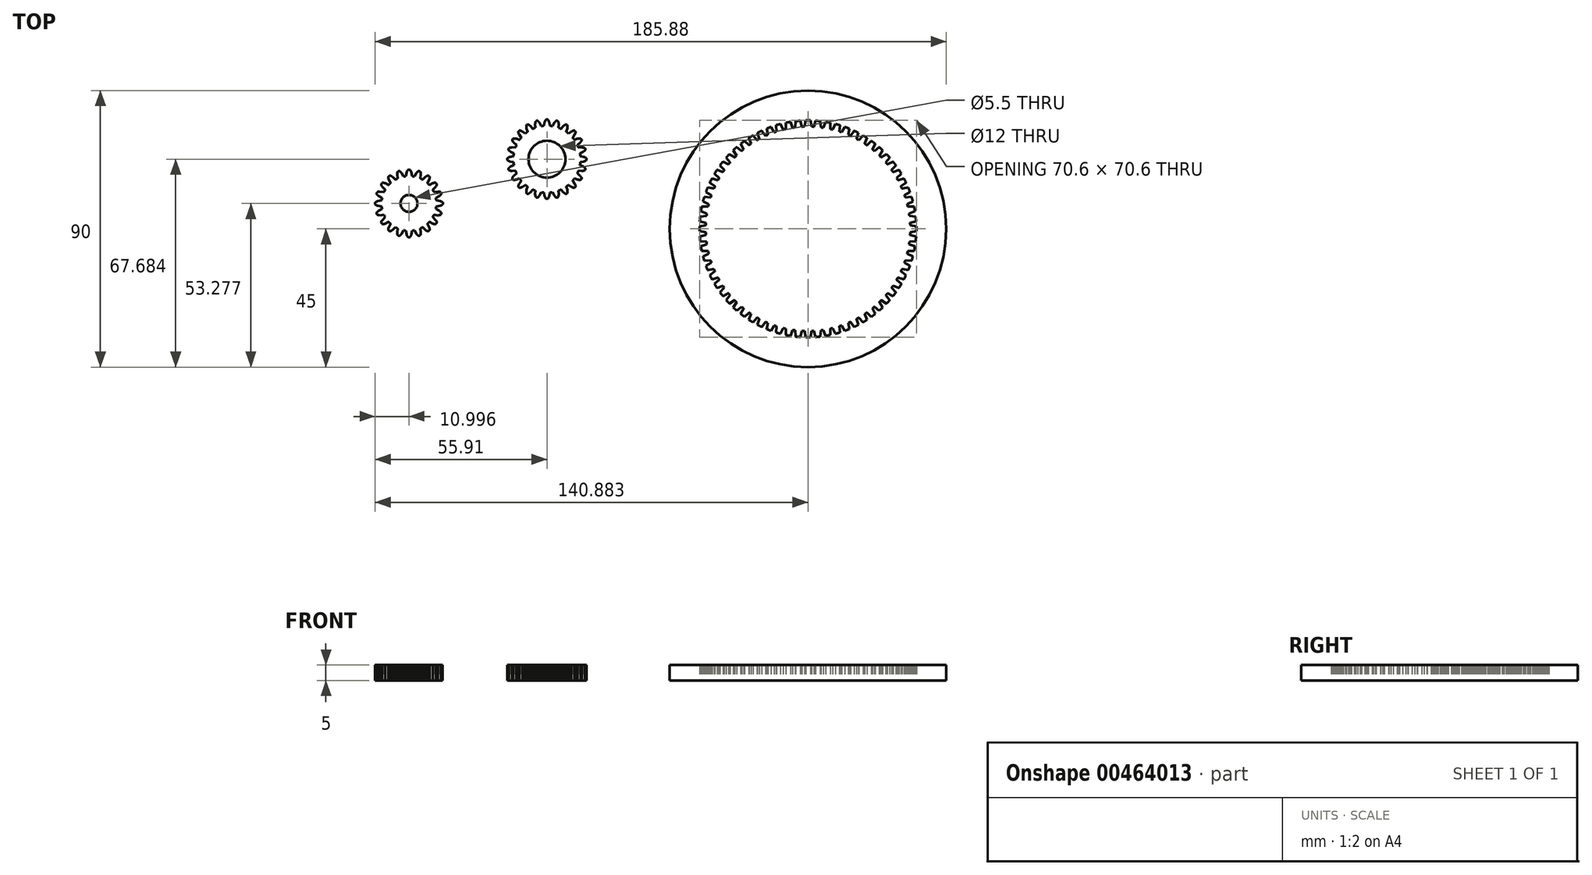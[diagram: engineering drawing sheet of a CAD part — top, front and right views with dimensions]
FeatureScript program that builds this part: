
annotation { "Feature Type Name" : "Feature", "Feature Type Description" : "" }
export const myFeature = defineFeature(function(context is Context, id is Id, definition is map)
    precondition{}
    {
        {
            var Q0;
            Q0=qCreatedBy(makeId("Top.planeOp"),FACE);
            var sketch = newSketch(context, id + "F0", { "sketchPlane" : qUnion([Q0])});
            skLineSegment(sketch, "E0.bottom", {"start": v(15.5, 15.5) * mm, "end": v(-15.5, 15.5) * mm, "construction": true});
            skLineSegment(sketch, "E0.top", {"start": v(15.5, -15.5) * mm, "end": v(-15.5, -15.5) * mm, "construction": true});
            skLineSegment(sketch, "E0.left", {"start": v(15.5, 15.5) * mm, "end": v(15.5, -15.5) * mm, "construction": true});
            skLineSegment(sketch, "E0.right", {"start": v(-15.5, 15.5) * mm, "end": v(-15.5, -15.5) * mm, "construction": true});
            skPoint(sketch, "E0.middle", {"position": v(0, 0) * mm});
            skCircle(sketch, "E1", {"center": v(0, 0) * mm, "radius": 10 * mm});
            skCircle(sketch, "E2", {"center": v(15.5, 15.5) * mm, "radius": 11.92 * mm});
            skCircle(sketch, "E3", {"center": v(15.5, -15.5) * mm, "radius": 11.92 * mm});
            skCircle(sketch, "E4", {"center": v(-15.5, -15.5) * mm, "radius": 11.92 * mm});
            skCircle(sketch, "E5", {"center": v(-15.5, 15.5) * mm, "radius": 11.92 * mm});
            skCircle(sketch, "E6", {"center": v(0, 0) * mm, "radius": 33.84 * mm});
            skCircle(sketch, "E7", {"center": v(0, 0) * mm, "radius": 11 * mm});
            skCircle(sketch, "E8", {"center": v(-15.5, 15.5) * mm, "radius": 12.92 * mm});
            skCircle(sketch, "E9", {"center": v(0, 0) * mm, "radius": 32.84 * mm});
            skPoint(sketch, "E10.center", {"position": v(-0.29, 2.68) * mm});
            skCircle(sketch, "E11", {"center": v(15.5, 15.5) * mm, "radius": 10.92 * mm, "construction": true});
            skCircle(sketch, "E12", {"center": v(15.5, -15.5) * mm, "radius": 10.92 * mm, "construction": true});
            skCircle(sketch, "E13", {"center": v(-15.5, -15.5) * mm, "radius": 10.92 * mm, "construction": true});
            skCircle(sketch, "E14", {"center": v(-15.5, 15.5) * mm, "radius": 10.92 * mm, "construction": true});
            skCircle(sketch, "E15", {"center": v(0, 0) * mm, "radius": 34.77 * mm, "construction": true});
            skCircle(sketch, "E16", {"center": v(0, 0) * mm, "radius": 8.93 * mm, "construction": true});
            skLineSegment(sketch, "E17", {"start": v(-0.79, 0) * mm, "end": v(-0.79, 9.97) * mm, "construction": true});
            skLineSegment(sketch, "E18", {"start": v(0.79, 0) * mm, "end": v(0.79, 9.97) * mm, "construction": true});
            skLineSegment(sketch, "E19", {"start": v(0.6, 10.98) * mm, "end": v(0.79, 9.97) * mm});
            skLineSegment(sketch, "E20", {"start": v(0.79, 9.97) * mm, "end": v(0.98, 8.87) * mm});
            skLineSegment(sketch, "E21", {"start": v(-0.79, 9.97) * mm, "end": v(-0.6, 10.98) * mm});
            skLineSegment(sketch, "E22", {"start": v(-0.6, 10.98) * mm, "end": v(-0.98, 8.87) * mm});
            skLineSegment(sketch, "E23.1.0", {"start": v(-3.98, 10.24) * mm, "end": v(-3.68, 8.12) * mm});
            skLineSegment(sketch, "E23.1.1", {"start": v(-2.83, 10.61) * mm, "end": v(-2.34, 9.7) * mm});
            skLineSegment(sketch, "E23.1.2", {"start": v(-2.34, 9.7) * mm, "end": v(-1.82, 8.72) * mm});
            skLineSegment(sketch, "E23.2.0", {"start": v(-6.96, 8.49) * mm, "end": v(-6.02, 6.56) * mm});
            skLineSegment(sketch, "E23.2.1", {"start": v(-5.98, 9.2) * mm, "end": v(-5.24, 8.49) * mm});
            skLineSegment(sketch, "E23.2.2", {"start": v(-5.24, 8.49) * mm, "end": v(-4.44, 7.71) * mm});
            skLineSegment(sketch, "E23.3.0", {"start": v(-9.25, 5.9) * mm, "end": v(-7.76, 4.36) * mm});
            skLineSegment(sketch, "E23.3.1", {"start": v(-8.54, 6.89) * mm, "end": v(-7.61, 6.43) * mm});
            skLineSegment(sketch, "E23.3.2", {"start": v(-7.61, 6.43) * mm, "end": v(-6.61, 5.95) * mm});
            skLineSegment(sketch, "E23.4.0", {"start": v(-10.63, 2.74) * mm, "end": v(-8.74, 1.73) * mm});
            skLineSegment(sketch, "E23.4.1", {"start": v(-10.26, 3.9) * mm, "end": v(-9.24, 3.75) * mm});
            skLineSegment(sketch, "E23.4.2", {"start": v(-9.24, 3.75) * mm, "end": v(-8.14, 3.6) * mm});
            skLineSegment(sketch, "E23.5.0", {"start": v(-10.97, -0.7) * mm, "end": v(-8.86, -1.07) * mm});
            skLineSegment(sketch, "E23.5.1", {"start": v(-10.97, 0.51) * mm, "end": v(-9.95, 0.7) * mm});
            skLineSegment(sketch, "E23.5.2", {"start": v(-9.95, 0.7) * mm, "end": v(-8.86, 0.88) * mm});
            skLineSegment(sketch, "E23.6.0", {"start": v(-10.22, -4.08) * mm, "end": v(-8.1, -3.78) * mm});
            skLineSegment(sketch, "E23.6.1", {"start": v(-10.6, -2.92) * mm, "end": v(-9.69, -2.44) * mm});
            skLineSegment(sketch, "E23.6.2", {"start": v(-9.69, -2.44) * mm, "end": v(-8.7, -1.92) * mm});
            skLineSegment(sketch, "E23.7.0", {"start": v(-8.47, -7.05) * mm, "end": v(-6.55, -6.11) * mm});
            skLineSegment(sketch, "E23.7.1", {"start": v(-9.19, -6.07) * mm, "end": v(-8.47, -5.33) * mm});
            skLineSegment(sketch, "E23.7.2", {"start": v(-8.47, -5.33) * mm, "end": v(-7.7, -4.53) * mm});
            skLineSegment(sketch, "E23.8.0", {"start": v(-5.89, -9.35) * mm, "end": v(-4.35, -7.86) * mm});
            skLineSegment(sketch, "E23.8.1", {"start": v(-6.87, -8.63) * mm, "end": v(-6.42, -7.7) * mm});
            skLineSegment(sketch, "E23.8.2", {"start": v(-6.42, -7.7) * mm, "end": v(-5.93, -6.7) * mm});
            skLineSegment(sketch, "E23.9.0", {"start": v(-2.72, -10.73) * mm, "end": v(-1.71, -8.84) * mm});
            skLineSegment(sketch, "E23.9.1", {"start": v(-3.87, -10.35) * mm, "end": v(-3.73, -9.33) * mm});
            skLineSegment(sketch, "E23.9.2", {"start": v(-3.73, -9.33) * mm, "end": v(-3.58, -8.23) * mm});
            skLineSegment(sketch, "E23.10.0", {"start": v(0.72, -11.06) * mm, "end": v(1.1, -8.95) * mm});
            skLineSegment(sketch, "E23.10.1", {"start": v(-0.5, -11.06) * mm, "end": v(-0.67, -10.05) * mm});
            skLineSegment(sketch, "E23.10.2", {"start": v(-0.67, -10.05) * mm, "end": v(-0.87, -8.95) * mm});
            skLineSegment(sketch, "E23.11.0", {"start": v(4.1, -10.32) * mm, "end": v(3.8, -8.2) * mm});
            skLineSegment(sketch, "E23.11.1", {"start": v(2.94, -10.7) * mm, "end": v(2.45, -9.78) * mm});
            skLineSegment(sketch, "E23.11.2", {"start": v(2.45, -9.78) * mm, "end": v(1.93, -8.8) * mm});
            skLineSegment(sketch, "E23.12.0", {"start": v(7.07, -8.57) * mm, "end": v(6.13, -6.64) * mm});
            skLineSegment(sketch, "E23.12.1", {"start": v(6.09, -9.28) * mm, "end": v(5.35, -8.56) * mm});
            skLineSegment(sketch, "E23.12.2", {"start": v(5.35, -8.56) * mm, "end": v(4.55, -7.8) * mm});
            skLineSegment(sketch, "E23.13.0", {"start": v(9.36, -5.98) * mm, "end": v(7.87, -4.44) * mm});
            skLineSegment(sketch, "E23.13.1", {"start": v(8.65, -6.96) * mm, "end": v(7.72, -6.51) * mm});
            skLineSegment(sketch, "E23.13.2", {"start": v(7.72, -6.51) * mm, "end": v(6.72, -6.02) * mm});
            skLineSegment(sketch, "E23.14.0", {"start": v(10.74, -2.82) * mm, "end": v(8.85, -1.8) * mm});
            skLineSegment(sketch, "E23.14.1", {"start": v(10.37, -3.97) * mm, "end": v(9.35, -3.83) * mm});
            skLineSegment(sketch, "E23.14.2", {"start": v(9.35, -3.83) * mm, "end": v(8.25, -3.67) * mm});
            skLineSegment(sketch, "E23.15.0", {"start": v(11.08, 0.62) * mm, "end": v(8.97, 1) * mm});
            skLineSegment(sketch, "E23.15.1", {"start": v(11.08, -0.59) * mm, "end": v(10.06, -0.77) * mm});
            skLineSegment(sketch, "E23.15.2", {"start": v(10.06, -0.77) * mm, "end": v(8.97, -0.96) * mm});
            skLineSegment(sketch, "E23.16.0", {"start": v(10.33, 4) * mm, "end": v(8.21, 3.7) * mm});
            skLineSegment(sketch, "E23.16.1", {"start": v(10.7, 2.84) * mm, "end": v(9.8, 2.36) * mm});
            skLineSegment(sketch, "E23.16.2", {"start": v(9.8, 2.36) * mm, "end": v(8.82, 1.84) * mm});
            skLineSegment(sketch, "E23.17.0", {"start": v(8.58, 6.98) * mm, "end": v(6.66, 6.04) * mm});
            skLineSegment(sketch, "E23.17.1", {"start": v(9.3, 6) * mm, "end": v(8.58, 5.25) * mm});
            skLineSegment(sketch, "E23.17.2", {"start": v(8.58, 5.25) * mm, "end": v(7.8, 4.45) * mm});
            skLineSegment(sketch, "E23.18.0", {"start": v(6, 9.27) * mm, "end": v(4.46, 7.78) * mm});
            skLineSegment(sketch, "E23.18.1", {"start": v(6.98, 8.55) * mm, "end": v(6.53, 7.63) * mm});
            skLineSegment(sketch, "E23.18.2", {"start": v(6.53, 7.63) * mm, "end": v(6.04, 6.63) * mm});
            skLineSegment(sketch, "E23.19.0", {"start": v(2.83, 10.65) * mm, "end": v(1.83, 8.76) * mm});
            skLineSegment(sketch, "E23.19.1", {"start": v(3.99, 10.27) * mm, "end": v(3.84, 9.25) * mm});
            skLineSegment(sketch, "E23.19.2", {"start": v(3.84, 9.25) * mm, "end": v(3.69, 8.15) * mm});
            skPoint(sketch, "E23.center", {"position": v(0.06, -0.04) * mm});
            skCircle(sketch, "E24.1.0", {"center": v(-15.5, -15.5) * mm, "radius": 12.92 * mm});
            skCircle(sketch, "E24.2.0", {"center": v(15.5, -15.5) * mm, "radius": 12.92 * mm});
            skCircle(sketch, "E24.3.0", {"center": v(15.5, 15.5) * mm, "radius": 12.92 * mm});
            skLineSegment(sketch, "E25.1.0", {"start": v(11.03, 5.48) * mm, "end": v(9.4, 4.07) * mm});
            skLineSegment(sketch, "E25.1.1", {"start": v(9.07, 6.59) * mm, "end": v(8.87, 5.58) * mm});
            skLineSegment(sketch, "E25.1.2", {"start": v(8.87, 5.58) * mm, "end": v(8.66, 4.48) * mm});
            skLineSegment(sketch, "E25.2.0", {"start": v(13.77, 4.66) * mm, "end": v(12.57, 2.88) * mm});
            skLineSegment(sketch, "E25.2.1", {"start": v(11.6, 5.23) * mm, "end": v(11.67, 4.2) * mm});
            skLineSegment(sketch, "E25.2.2", {"start": v(11.67, 4.2) * mm, "end": v(11.74, 3.09) * mm});
            skLineSegment(sketch, "E25.3.0", {"start": v(16.64, 4.58) * mm, "end": v(15.94, 2.56) * mm});
            skLineSegment(sketch, "E25.3.1", {"start": v(14.39, 4.56) * mm, "end": v(14.72, 3.6) * mm});
            skLineSegment(sketch, "E25.3.2", {"start": v(14.72, 3.6) * mm, "end": v(15.08, 2.54) * mm});
            skLineSegment(sketch, "E25.4.0", {"start": v(19.42, 5.25) * mm, "end": v(19.27, 3.11) * mm});
            skLineSegment(sketch, "E25.4.1", {"start": v(17.26, 4.65) * mm, "end": v(17.83, 3.8) * mm});
            skLineSegment(sketch, "E25.4.2", {"start": v(17.83, 3.8) * mm, "end": v(18.45, 2.87) * mm});
            skLineSegment(sketch, "E25.5.0", {"start": v(21.94, 6.61) * mm, "end": v(22.35, 4.51) * mm});
            skLineSegment(sketch, "E25.5.1", {"start": v(20, 5.47) * mm, "end": v(20.78, 4.8) * mm});
            skLineSegment(sketch, "E25.5.2", {"start": v(20.78, 4.8) * mm, "end": v(21.62, 4.07) * mm});
            skLineSegment(sketch, "E25.6.0", {"start": v(24.02, 8.58) * mm, "end": v(24.96, 6.66) * mm});
            skLineSegment(sketch, "E25.6.1", {"start": v(22.45, 6.98) * mm, "end": v(23.37, 6.53) * mm});
            skLineSegment(sketch, "E25.6.2", {"start": v(23.37, 6.53) * mm, "end": v(24.37, 6.04) * mm});
            skLineSegment(sketch, "E25.7.0", {"start": v(25.52, 11.03) * mm, "end": v(26.93, 9.4) * mm});
            skLineSegment(sketch, "E25.7.1", {"start": v(24.41, 9.07) * mm, "end": v(25.42, 8.87) * mm});
            skLineSegment(sketch, "E25.7.2", {"start": v(25.42, 8.87) * mm, "end": v(26.52, 8.66) * mm});
            skLineSegment(sketch, "E25.8.0", {"start": v(26.34, 13.77) * mm, "end": v(28.12, 12.57) * mm});
            skLineSegment(sketch, "E25.8.1", {"start": v(25.77, 11.6) * mm, "end": v(26.8, 11.67) * mm});
            skLineSegment(sketch, "E25.8.2", {"start": v(26.8, 11.67) * mm, "end": v(27.91, 11.74) * mm});
            skLineSegment(sketch, "E25.9.0", {"start": v(26.42, 16.64) * mm, "end": v(28.44, 15.94) * mm});
            skLineSegment(sketch, "E25.9.1", {"start": v(26.44, 14.39) * mm, "end": v(27.4, 14.72) * mm});
            skLineSegment(sketch, "E25.9.2", {"start": v(27.4, 14.72) * mm, "end": v(28.46, 15.08) * mm});
            skLineSegment(sketch, "E25.10.0", {"start": v(25.75, 19.42) * mm, "end": v(27.89, 19.27) * mm});
            skLineSegment(sketch, "E25.10.1", {"start": v(26.35, 17.26) * mm, "end": v(27.2, 17.83) * mm});
            skLineSegment(sketch, "E25.10.2", {"start": v(27.2, 17.83) * mm, "end": v(28.13, 18.45) * mm});
            skLineSegment(sketch, "E25.11.0", {"start": v(24.39, 21.94) * mm, "end": v(26.49, 22.35) * mm});
            skLineSegment(sketch, "E25.11.1", {"start": v(25.53, 20) * mm, "end": v(26.2, 20.78) * mm});
            skLineSegment(sketch, "E25.11.2", {"start": v(26.2, 20.78) * mm, "end": v(26.93, 21.62) * mm});
            skLineSegment(sketch, "E25.12.0", {"start": v(22.42, 24.02) * mm, "end": v(24.34, 24.96) * mm});
            skLineSegment(sketch, "E25.12.1", {"start": v(24.02, 22.45) * mm, "end": v(24.47, 23.37) * mm});
            skLineSegment(sketch, "E25.12.2", {"start": v(24.47, 23.37) * mm, "end": v(24.96, 24.37) * mm});
            skLineSegment(sketch, "E25.13.0", {"start": v(19.97, 25.52) * mm, "end": v(21.6, 26.93) * mm});
            skLineSegment(sketch, "E25.13.1", {"start": v(21.93, 24.41) * mm, "end": v(22.13, 25.42) * mm});
            skLineSegment(sketch, "E25.13.2", {"start": v(22.13, 25.42) * mm, "end": v(22.34, 26.52) * mm});
            skLineSegment(sketch, "E25.14.0", {"start": v(17.23, 26.34) * mm, "end": v(18.43, 28.12) * mm});
            skLineSegment(sketch, "E25.14.1", {"start": v(19.4, 25.77) * mm, "end": v(19.33, 26.8) * mm});
            skLineSegment(sketch, "E25.14.2", {"start": v(19.33, 26.8) * mm, "end": v(19.26, 27.91) * mm});
            skLineSegment(sketch, "E25.15.0", {"start": v(14.36, 26.42) * mm, "end": v(15.06, 28.44) * mm});
            skLineSegment(sketch, "E25.15.1", {"start": v(16.61, 26.44) * mm, "end": v(16.28, 27.4) * mm});
            skLineSegment(sketch, "E25.15.2", {"start": v(16.28, 27.4) * mm, "end": v(15.92, 28.46) * mm});
            skLineSegment(sketch, "E25.16.0", {"start": v(11.58, 25.75) * mm, "end": v(11.73, 27.89) * mm});
            skLineSegment(sketch, "E25.16.1", {"start": v(13.74, 26.35) * mm, "end": v(13.17, 27.2) * mm});
            skLineSegment(sketch, "E25.16.2", {"start": v(13.17, 27.2) * mm, "end": v(12.55, 28.13) * mm});
            skLineSegment(sketch, "E25.17.0", {"start": v(9.06, 24.39) * mm, "end": v(8.65, 26.49) * mm});
            skLineSegment(sketch, "E25.17.1", {"start": v(11, 25.53) * mm, "end": v(10.22, 26.2) * mm});
            skLineSegment(sketch, "E25.17.2", {"start": v(10.22, 26.2) * mm, "end": v(9.38, 26.93) * mm});
            skLineSegment(sketch, "E25.18.0", {"start": v(6.98, 22.42) * mm, "end": v(6.04, 24.34) * mm});
            skLineSegment(sketch, "E25.18.1", {"start": v(8.55, 24.02) * mm, "end": v(7.63, 24.47) * mm});
            skLineSegment(sketch, "E25.18.2", {"start": v(7.63, 24.47) * mm, "end": v(6.63, 24.96) * mm});
            skLineSegment(sketch, "E25.19.0", {"start": v(5.48, 19.97) * mm, "end": v(4.07, 21.6) * mm});
            skLineSegment(sketch, "E25.19.1", {"start": v(6.59, 21.93) * mm, "end": v(5.58, 22.13) * mm});
            skLineSegment(sketch, "E25.19.2", {"start": v(5.58, 22.13) * mm, "end": v(4.48, 22.34) * mm});
            skLineSegment(sketch, "E25.20.0", {"start": v(4.66, 17.23) * mm, "end": v(2.88, 18.43) * mm});
            skLineSegment(sketch, "E25.20.1", {"start": v(5.23, 19.4) * mm, "end": v(4.2, 19.33) * mm});
            skLineSegment(sketch, "E25.20.2", {"start": v(4.2, 19.33) * mm, "end": v(3.09, 19.26) * mm});
            skLineSegment(sketch, "E25.21.0", {"start": v(4.58, 14.36) * mm, "end": v(2.56, 15.06) * mm});
            skLineSegment(sketch, "E25.21.1", {"start": v(4.56, 16.61) * mm, "end": v(3.6, 16.28) * mm});
            skLineSegment(sketch, "E25.21.2", {"start": v(3.6, 16.28) * mm, "end": v(2.54, 15.92) * mm});
            skLineSegment(sketch, "E25.22.0", {"start": v(5.25, 11.58) * mm, "end": v(3.11, 11.73) * mm});
            skLineSegment(sketch, "E25.22.1", {"start": v(4.65, 13.74) * mm, "end": v(3.8, 13.17) * mm});
            skLineSegment(sketch, "E25.22.2", {"start": v(3.8, 13.17) * mm, "end": v(2.87, 12.55) * mm});
            skLineSegment(sketch, "E25.23.0", {"start": v(6.61, 9.06) * mm, "end": v(4.51, 8.65) * mm});
            skLineSegment(sketch, "E25.23.1", {"start": v(5.47, 11) * mm, "end": v(4.8, 10.22) * mm});
            skLineSegment(sketch, "E25.23.2", {"start": v(4.8, 10.22) * mm, "end": v(4.07, 9.38) * mm});
            skLineSegment(sketch, "E26.1.0", {"start": v(-6.55, 8.98) * mm, "end": v(-5.53, 8.78) * mm});
            skLineSegment(sketch, "E26.1.1", {"start": v(-5.53, 8.78) * mm, "end": v(-4.44, 8.57) * mm});
            skLineSegment(sketch, "E26.1.2", {"start": v(-5.44, 10.94) * mm, "end": v(-4.03, 9.32) * mm});
            skLineSegment(sketch, "E26.2.0", {"start": v(-5.16, 11.52) * mm, "end": v(-4.14, 11.6) * mm});
            skLineSegment(sketch, "E26.2.1", {"start": v(-4.14, 11.6) * mm, "end": v(-3.03, 11.67) * mm});
            skLineSegment(sketch, "E26.2.2", {"start": v(-4.6, 13.7) * mm, "end": v(-2.82, 12.5) * mm});
            skLineSegment(sketch, "E26.3.0", {"start": v(-4.49, 14.33) * mm, "end": v(-3.51, 14.67) * mm});
            skLineSegment(sketch, "E26.3.1", {"start": v(-3.51, 14.67) * mm, "end": v(-2.46, 15.03) * mm});
            skLineSegment(sketch, "E26.3.2", {"start": v(-4.5, 16.58) * mm, "end": v(-2.48, 15.88) * mm});
            skLineSegment(sketch, "E26.4.0", {"start": v(-4.56, 17.22) * mm, "end": v(-3.7, 17.8) * mm});
            skLineSegment(sketch, "E26.4.1", {"start": v(-3.7, 17.8) * mm, "end": v(-2.78, 18.42) * mm});
            skLineSegment(sketch, "E26.4.2", {"start": v(-5.16, 19.4) * mm, "end": v(-3.02, 19.24) * mm});
            skLineSegment(sketch, "E26.5.0", {"start": v(-5.38, 20) * mm, "end": v(-4.7, 20.77) * mm});
            skLineSegment(sketch, "E26.5.1", {"start": v(-4.7, 20.77) * mm, "end": v(-3.97, 21.61) * mm});
            skLineSegment(sketch, "E26.5.2", {"start": v(-6.52, 21.94) * mm, "end": v(-4.41, 22.34) * mm});
            skLineSegment(sketch, "E26.6.0", {"start": v(-6.89, 22.46) * mm, "end": v(-6.43, 23.39) * mm});
            skLineSegment(sketch, "E26.6.1", {"start": v(-6.43, 23.39) * mm, "end": v(-5.95, 24.39) * mm});
            skLineSegment(sketch, "E26.6.2", {"start": v(-8.49, 24.04) * mm, "end": v(-6.56, 24.98) * mm});
            skLineSegment(sketch, "E26.7.0", {"start": v(-8.98, 24.45) * mm, "end": v(-8.78, 25.47) * mm});
            skLineSegment(sketch, "E26.7.1", {"start": v(-8.78, 25.47) * mm, "end": v(-8.57, 26.56) * mm});
            skLineSegment(sketch, "E26.7.2", {"start": v(-10.94, 25.56) * mm, "end": v(-9.32, 26.97) * mm});
            skLineSegment(sketch, "E26.8.0", {"start": v(-11.52, 25.84) * mm, "end": v(-11.6, 26.86) * mm});
            skLineSegment(sketch, "E26.8.1", {"start": v(-11.6, 26.86) * mm, "end": v(-11.67, 27.97) * mm});
            skLineSegment(sketch, "E26.8.2", {"start": v(-13.7, 26.4) * mm, "end": v(-12.5, 28.18) * mm});
            skLineSegment(sketch, "E26.9.0", {"start": v(-14.33, 26.51) * mm, "end": v(-14.67, 27.49) * mm});
            skLineSegment(sketch, "E26.9.1", {"start": v(-14.67, 27.49) * mm, "end": v(-15.03, 28.54) * mm});
            skLineSegment(sketch, "E26.9.2", {"start": v(-16.58, 26.5) * mm, "end": v(-15.88, 28.52) * mm});
            skLineSegment(sketch, "E26.10.0", {"start": v(-17.22, 26.44) * mm, "end": v(-17.8, 27.3) * mm});
            skLineSegment(sketch, "E26.10.1", {"start": v(-17.8, 27.3) * mm, "end": v(-18.42, 28.22) * mm});
            skLineSegment(sketch, "E26.10.2", {"start": v(-19.4, 25.84) * mm, "end": v(-19.24, 27.98) * mm});
            skLineSegment(sketch, "E26.11.0", {"start": v(-20, 25.62) * mm, "end": v(-20.77, 26.3) * mm});
            skLineSegment(sketch, "E26.11.1", {"start": v(-20.77, 26.3) * mm, "end": v(-21.61, 27.03) * mm});
            skLineSegment(sketch, "E26.11.2", {"start": v(-21.94, 24.48) * mm, "end": v(-22.34, 26.59) * mm});
            skLineSegment(sketch, "E26.12.0", {"start": v(-22.46, 24.11) * mm, "end": v(-23.39, 24.57) * mm});
            skLineSegment(sketch, "E26.12.1", {"start": v(-23.39, 24.57) * mm, "end": v(-24.39, 25.05) * mm});
            skLineSegment(sketch, "E26.12.2", {"start": v(-24.04, 22.51) * mm, "end": v(-24.98, 24.44) * mm});
            skLineSegment(sketch, "E26.13.0", {"start": v(-24.45, 22.02) * mm, "end": v(-25.47, 22.22) * mm});
            skLineSegment(sketch, "E26.13.1", {"start": v(-25.47, 22.22) * mm, "end": v(-26.56, 22.43) * mm});
            skLineSegment(sketch, "E26.13.2", {"start": v(-25.56, 20.06) * mm, "end": v(-26.97, 21.68) * mm});
            skLineSegment(sketch, "E26.14.0", {"start": v(-25.84, 19.48) * mm, "end": v(-26.86, 19.4) * mm});
            skLineSegment(sketch, "E26.14.1", {"start": v(-26.86, 19.4) * mm, "end": v(-27.97, 19.33) * mm});
            skLineSegment(sketch, "E26.14.2", {"start": v(-26.4, 17.3) * mm, "end": v(-28.18, 18.5) * mm});
            skLineSegment(sketch, "E26.15.0", {"start": v(-26.51, 16.67) * mm, "end": v(-27.49, 16.33) * mm});
            skLineSegment(sketch, "E26.15.1", {"start": v(-27.49, 16.33) * mm, "end": v(-28.54, 15.97) * mm});
            skLineSegment(sketch, "E26.15.2", {"start": v(-26.5, 14.42) * mm, "end": v(-28.52, 15.12) * mm});
            skLineSegment(sketch, "E26.16.0", {"start": v(-26.44, 13.78) * mm, "end": v(-27.3, 13.2) * mm});
            skLineSegment(sketch, "E26.16.1", {"start": v(-27.3, 13.2) * mm, "end": v(-28.22, 12.58) * mm});
            skLineSegment(sketch, "E26.16.2", {"start": v(-25.84, 11.6) * mm, "end": v(-27.98, 11.76) * mm});
            skLineSegment(sketch, "E26.17.0", {"start": v(-25.62, 11) * mm, "end": v(-26.3, 10.23) * mm});
            skLineSegment(sketch, "E26.17.1", {"start": v(-26.3, 10.23) * mm, "end": v(-27.03, 9.39) * mm});
            skLineSegment(sketch, "E26.17.2", {"start": v(-24.48, 9.06) * mm, "end": v(-26.59, 8.66) * mm});
            skLineSegment(sketch, "E26.18.0", {"start": v(-24.11, 8.54) * mm, "end": v(-24.57, 7.61) * mm});
            skLineSegment(sketch, "E26.18.1", {"start": v(-24.57, 7.61) * mm, "end": v(-25.05, 6.61) * mm});
            skLineSegment(sketch, "E26.18.2", {"start": v(-22.51, 6.96) * mm, "end": v(-24.44, 6.02) * mm});
            skLineSegment(sketch, "E26.19.0", {"start": v(-22.02, 6.55) * mm, "end": v(-22.22, 5.53) * mm});
            skLineSegment(sketch, "E26.19.1", {"start": v(-22.22, 5.53) * mm, "end": v(-22.43, 4.44) * mm});
            skLineSegment(sketch, "E26.19.2", {"start": v(-20.06, 5.44) * mm, "end": v(-21.68, 4.03) * mm});
            skLineSegment(sketch, "E26.20.0", {"start": v(-19.48, 5.16) * mm, "end": v(-19.4, 4.14) * mm});
            skLineSegment(sketch, "E26.20.1", {"start": v(-19.4, 4.14) * mm, "end": v(-19.33, 3.03) * mm});
            skLineSegment(sketch, "E26.20.2", {"start": v(-17.3, 4.6) * mm, "end": v(-18.5, 2.82) * mm});
            skLineSegment(sketch, "E26.21.0", {"start": v(-16.67, 4.49) * mm, "end": v(-16.33, 3.51) * mm});
            skLineSegment(sketch, "E26.21.1", {"start": v(-16.33, 3.51) * mm, "end": v(-15.97, 2.46) * mm});
            skLineSegment(sketch, "E26.21.2", {"start": v(-14.42, 4.5) * mm, "end": v(-15.12, 2.48) * mm});
            skLineSegment(sketch, "E26.22.0", {"start": v(-13.78, 4.56) * mm, "end": v(-13.2, 3.7) * mm});
            skLineSegment(sketch, "E26.22.1", {"start": v(-13.2, 3.7) * mm, "end": v(-12.58, 2.78) * mm});
            skLineSegment(sketch, "E26.22.2", {"start": v(-11.6, 5.16) * mm, "end": v(-11.76, 3.02) * mm});
            skLineSegment(sketch, "E26.23.0", {"start": v(-11, 5.38) * mm, "end": v(-10.23, 4.7) * mm});
            skLineSegment(sketch, "E26.23.1", {"start": v(-10.23, 4.7) * mm, "end": v(-9.39, 3.97) * mm});
            skLineSegment(sketch, "E26.23.2", {"start": v(-9.06, 6.52) * mm, "end": v(-8.66, 4.41) * mm});
            skLineSegment(sketch, "E27.1.0", {"start": v(-10.9, -5.52) * mm, "end": v(-9.28, -4.12) * mm});
            skLineSegment(sketch, "E27.1.1", {"start": v(-8.94, -6.63) * mm, "end": v(-8.74, -5.62) * mm});
            skLineSegment(sketch, "E27.1.2", {"start": v(-8.74, -5.62) * mm, "end": v(-8.53, -4.53) * mm});
            skLineSegment(sketch, "E27.2.0", {"start": v(-13.64, -4.67) * mm, "end": v(-12.44, -2.9) * mm});
            skLineSegment(sketch, "E27.2.1", {"start": v(-11.46, -5.24) * mm, "end": v(-11.53, -4.2) * mm});
            skLineSegment(sketch, "E27.2.2", {"start": v(-11.53, -4.2) * mm, "end": v(-11.6, -3.1) * mm});
            skLineSegment(sketch, "E27.3.0", {"start": v(-16.5, -4.56) * mm, "end": v(-15.8, -2.53) * mm});
            skLineSegment(sketch, "E27.3.1", {"start": v(-14.25, -4.54) * mm, "end": v(-14.59, -3.57) * mm});
            skLineSegment(sketch, "E27.3.2", {"start": v(-14.59, -3.57) * mm, "end": v(-14.95, -2.52) * mm});
            skLineSegment(sketch, "E27.4.0", {"start": v(-19.3, -5.2) * mm, "end": v(-19.15, -3.05) * mm});
            skLineSegment(sketch, "E27.4.1", {"start": v(-17.13, -4.6) * mm, "end": v(-17.7, -3.74) * mm});
            skLineSegment(sketch, "E27.4.2", {"start": v(-17.7, -3.74) * mm, "end": v(-18.33, -2.82) * mm});
            skLineSegment(sketch, "E27.5.0", {"start": v(-21.84, -6.53) * mm, "end": v(-22.25, -4.42) * mm});
            skLineSegment(sketch, "E27.5.1", {"start": v(-19.9, -5.39) * mm, "end": v(-20.68, -4.7) * mm});
            skLineSegment(sketch, "E27.5.2", {"start": v(-20.68, -4.7) * mm, "end": v(-21.52, -3.98) * mm});
            skLineSegment(sketch, "E27.6.0", {"start": v(-23.95, -8.47) * mm, "end": v(-24.89, -6.55) * mm});
            skLineSegment(sketch, "E27.6.1", {"start": v(-22.37, -6.87) * mm, "end": v(-23.3, -6.42) * mm});
            skLineSegment(sketch, "E27.6.2", {"start": v(-23.3, -6.42) * mm, "end": v(-24.3, -5.93) * mm});
            skLineSegment(sketch, "E27.7.0", {"start": v(-25.48, -10.9) * mm, "end": v(-26.88, -9.28) * mm});
            skLineSegment(sketch, "E27.7.1", {"start": v(-24.37, -8.94) * mm, "end": v(-25.38, -8.74) * mm});
            skLineSegment(sketch, "E27.7.2", {"start": v(-25.38, -8.74) * mm, "end": v(-26.47, -8.53) * mm});
            skLineSegment(sketch, "E27.8.0", {"start": v(-26.33, -13.64) * mm, "end": v(-28.1, -12.44) * mm});
            skLineSegment(sketch, "E27.8.1", {"start": v(-25.76, -11.46) * mm, "end": v(-26.8, -11.53) * mm});
            skLineSegment(sketch, "E27.8.2", {"start": v(-26.8, -11.53) * mm, "end": v(-27.9, -11.6) * mm});
            skLineSegment(sketch, "E27.9.0", {"start": v(-26.44, -16.5) * mm, "end": v(-28.47, -15.8) * mm});
            skLineSegment(sketch, "E27.9.1", {"start": v(-26.46, -14.25) * mm, "end": v(-27.43, -14.59) * mm});
            skLineSegment(sketch, "E27.9.2", {"start": v(-27.43, -14.59) * mm, "end": v(-28.48, -14.95) * mm});
            skLineSegment(sketch, "E27.10.0", {"start": v(-25.8, -19.3) * mm, "end": v(-27.95, -19.15) * mm});
            skLineSegment(sketch, "E27.10.1", {"start": v(-26.4, -17.13) * mm, "end": v(-27.26, -17.7) * mm});
            skLineSegment(sketch, "E27.10.2", {"start": v(-27.26, -17.7) * mm, "end": v(-28.18, -18.33) * mm});
            skLineSegment(sketch, "E27.11.0", {"start": v(-24.47, -21.84) * mm, "end": v(-26.58, -22.25) * mm});
            skLineSegment(sketch, "E27.11.1", {"start": v(-25.61, -19.9) * mm, "end": v(-26.3, -20.68) * mm});
            skLineSegment(sketch, "E27.11.2", {"start": v(-26.3, -20.68) * mm, "end": v(-27.02, -21.52) * mm});
            skLineSegment(sketch, "E27.12.0", {"start": v(-22.53, -23.95) * mm, "end": v(-24.45, -24.89) * mm});
            skLineSegment(sketch, "E27.12.1", {"start": v(-24.13, -22.37) * mm, "end": v(-24.58, -23.3) * mm});
            skLineSegment(sketch, "E27.12.2", {"start": v(-24.58, -23.3) * mm, "end": v(-25.07, -24.3) * mm});
            skLineSegment(sketch, "E27.13.0", {"start": v(-20.1, -25.48) * mm, "end": v(-21.72, -26.88) * mm});
            skLineSegment(sketch, "E27.13.1", {"start": v(-22.06, -24.37) * mm, "end": v(-22.26, -25.38) * mm});
            skLineSegment(sketch, "E27.13.2", {"start": v(-22.26, -25.38) * mm, "end": v(-22.47, -26.47) * mm});
            skLineSegment(sketch, "E27.14.0", {"start": v(-17.36, -26.33) * mm, "end": v(-18.56, -28.1) * mm});
            skLineSegment(sketch, "E27.14.1", {"start": v(-19.54, -25.76) * mm, "end": v(-19.47, -26.8) * mm});
            skLineSegment(sketch, "E27.14.2", {"start": v(-19.47, -26.8) * mm, "end": v(-19.4, -27.9) * mm});
            skLineSegment(sketch, "E27.15.0", {"start": v(-14.5, -26.44) * mm, "end": v(-15.2, -28.47) * mm});
            skLineSegment(sketch, "E27.15.1", {"start": v(-16.75, -26.46) * mm, "end": v(-16.41, -27.43) * mm});
            skLineSegment(sketch, "E27.15.2", {"start": v(-16.41, -27.43) * mm, "end": v(-16.05, -28.48) * mm});
            skLineSegment(sketch, "E27.16.0", {"start": v(-11.7, -25.8) * mm, "end": v(-11.85, -27.95) * mm});
            skLineSegment(sketch, "E27.16.1", {"start": v(-13.87, -26.4) * mm, "end": v(-13.3, -27.26) * mm});
            skLineSegment(sketch, "E27.16.2", {"start": v(-13.3, -27.26) * mm, "end": v(-12.67, -28.18) * mm});
            skLineSegment(sketch, "E27.17.0", {"start": v(-9.16, -24.47) * mm, "end": v(-8.75, -26.58) * mm});
            skLineSegment(sketch, "E27.17.1", {"start": v(-11.1, -25.61) * mm, "end": v(-10.32, -26.3) * mm});
            skLineSegment(sketch, "E27.17.2", {"start": v(-10.32, -26.3) * mm, "end": v(-9.48, -27.02) * mm});
            skLineSegment(sketch, "E27.18.0", {"start": v(-7.05, -22.53) * mm, "end": v(-6.11, -24.45) * mm});
            skLineSegment(sketch, "E27.18.1", {"start": v(-8.63, -24.13) * mm, "end": v(-7.7, -24.58) * mm});
            skLineSegment(sketch, "E27.18.2", {"start": v(-7.7, -24.58) * mm, "end": v(-6.7, -25.07) * mm});
            skLineSegment(sketch, "E27.19.0", {"start": v(-5.52, -20.1) * mm, "end": v(-4.12, -21.72) * mm});
            skLineSegment(sketch, "E27.19.1", {"start": v(-6.63, -22.06) * mm, "end": v(-5.62, -22.26) * mm});
            skLineSegment(sketch, "E27.19.2", {"start": v(-5.62, -22.26) * mm, "end": v(-4.53, -22.47) * mm});
            skLineSegment(sketch, "E27.20.0", {"start": v(-4.67, -17.36) * mm, "end": v(-2.9, -18.56) * mm});
            skLineSegment(sketch, "E27.20.1", {"start": v(-5.24, -19.54) * mm, "end": v(-4.2, -19.47) * mm});
            skLineSegment(sketch, "E27.20.2", {"start": v(-4.2, -19.47) * mm, "end": v(-3.1, -19.4) * mm});
            skLineSegment(sketch, "E27.21.0", {"start": v(-4.56, -14.5) * mm, "end": v(-2.53, -15.2) * mm});
            skLineSegment(sketch, "E27.21.1", {"start": v(-4.54, -16.75) * mm, "end": v(-3.57, -16.41) * mm});
            skLineSegment(sketch, "E27.21.2", {"start": v(-3.57, -16.41) * mm, "end": v(-2.52, -16.05) * mm});
            skLineSegment(sketch, "E27.22.0", {"start": v(-5.2, -11.7) * mm, "end": v(-3.05, -11.85) * mm});
            skLineSegment(sketch, "E27.22.1", {"start": v(-4.6, -13.87) * mm, "end": v(-3.74, -13.3) * mm});
            skLineSegment(sketch, "E27.22.2", {"start": v(-3.74, -13.3) * mm, "end": v(-2.82, -12.67) * mm});
            skLineSegment(sketch, "E27.23.0", {"start": v(-6.53, -9.16) * mm, "end": v(-4.42, -8.75) * mm});
            skLineSegment(sketch, "E27.23.1", {"start": v(-5.39, -11.1) * mm, "end": v(-4.7, -10.32) * mm});
            skLineSegment(sketch, "E27.23.2", {"start": v(-4.7, -10.32) * mm, "end": v(-3.98, -9.48) * mm});
            skLineSegment(sketch, "E28.1.0", {"start": v(5.56, -10.98) * mm, "end": v(4.16, -9.37) * mm});
            skLineSegment(sketch, "E28.1.1", {"start": v(5.66, -8.83) * mm, "end": v(4.57, -8.62) * mm});
            skLineSegment(sketch, "E28.1.2", {"start": v(6.67, -9.03) * mm, "end": v(5.66, -8.83) * mm});
            skLineSegment(sketch, "E28.2.0", {"start": v(4.73, -13.71) * mm, "end": v(2.96, -12.51) * mm});
            skLineSegment(sketch, "E28.2.1", {"start": v(4.27, -11.6) * mm, "end": v(3.16, -11.68) * mm});
            skLineSegment(sketch, "E28.2.2", {"start": v(5.3, -11.53) * mm, "end": v(4.27, -11.6) * mm});
            skLineSegment(sketch, "E28.3.0", {"start": v(4.64, -16.56) * mm, "end": v(2.61, -15.86) * mm});
            skLineSegment(sketch, "E28.3.1", {"start": v(3.65, -14.64) * mm, "end": v(2.6, -15) * mm});
            skLineSegment(sketch, "E28.3.2", {"start": v(4.62, -14.3) * mm, "end": v(3.65, -14.64) * mm});
            skLineSegment(sketch, "E28.4.0", {"start": v(5.28, -19.33) * mm, "end": v(3.14, -19.18) * mm});
            skLineSegment(sketch, "E28.4.1", {"start": v(3.83, -17.74) * mm, "end": v(2.9, -18.36) * mm});
            skLineSegment(sketch, "E28.4.2", {"start": v(4.68, -17.16) * mm, "end": v(3.83, -17.74) * mm});
            skLineSegment(sketch, "E28.5.0", {"start": v(6.62, -21.85) * mm, "end": v(4.52, -22.26) * mm});
            skLineSegment(sketch, "E28.5.1", {"start": v(4.8, -20.69) * mm, "end": v(4.08, -21.52) * mm});
            skLineSegment(sketch, "E28.5.2", {"start": v(5.48, -19.9) * mm, "end": v(4.8, -20.69) * mm});
            skLineSegment(sketch, "E28.6.0", {"start": v(8.57, -23.93) * mm, "end": v(6.64, -24.87) * mm});
            skLineSegment(sketch, "E28.6.1", {"start": v(6.51, -23.28) * mm, "end": v(6.02, -24.28) * mm});
            skLineSegment(sketch, "E28.6.2", {"start": v(6.96, -22.35) * mm, "end": v(6.51, -23.28) * mm});
            skLineSegment(sketch, "E28.7.0", {"start": v(10.98, -25.44) * mm, "end": v(9.37, -26.84) * mm});
            skLineSegment(sketch, "E28.7.1", {"start": v(8.83, -25.34) * mm, "end": v(8.62, -26.43) * mm});
            skLineSegment(sketch, "E28.7.2", {"start": v(9.03, -24.33) * mm, "end": v(8.83, -25.34) * mm});
            skLineSegment(sketch, "E28.8.0", {"start": v(13.71, -26.27) * mm, "end": v(12.51, -28.04) * mm});
            skLineSegment(sketch, "E28.8.1", {"start": v(11.6, -26.73) * mm, "end": v(11.68, -27.84) * mm});
            skLineSegment(sketch, "E28.8.2", {"start": v(11.53, -25.7) * mm, "end": v(11.6, -26.73) * mm});
            skLineSegment(sketch, "E28.9.0", {"start": v(16.56, -26.36) * mm, "end": v(15.86, -28.39) * mm});
            skLineSegment(sketch, "E28.9.1", {"start": v(14.64, -27.35) * mm, "end": v(15, -28.4) * mm});
            skLineSegment(sketch, "E28.9.2", {"start": v(14.3, -26.38) * mm, "end": v(14.64, -27.35) * mm});
            skLineSegment(sketch, "E28.10.0", {"start": v(19.33, -25.72) * mm, "end": v(19.18, -27.86) * mm});
            skLineSegment(sketch, "E28.10.1", {"start": v(17.74, -27.17) * mm, "end": v(18.36, -28.1) * mm});
            skLineSegment(sketch, "E28.10.2", {"start": v(17.16, -26.32) * mm, "end": v(17.74, -27.17) * mm});
            skLineSegment(sketch, "E28.11.0", {"start": v(21.85, -24.38) * mm, "end": v(22.26, -26.48) * mm});
            skLineSegment(sketch, "E28.11.1", {"start": v(20.69, -26.2) * mm, "end": v(21.52, -26.92) * mm});
            skLineSegment(sketch, "E28.11.2", {"start": v(19.9, -25.52) * mm, "end": v(20.69, -26.2) * mm});
            skLineSegment(sketch, "E28.12.0", {"start": v(23.93, -22.43) * mm, "end": v(24.87, -24.36) * mm});
            skLineSegment(sketch, "E28.12.1", {"start": v(23.28, -24.49) * mm, "end": v(24.28, -24.98) * mm});
            skLineSegment(sketch, "E28.12.2", {"start": v(22.35, -24.04) * mm, "end": v(23.28, -24.49) * mm});
            skLineSegment(sketch, "E28.13.0", {"start": v(25.44, -20.02) * mm, "end": v(26.84, -21.63) * mm});
            skLineSegment(sketch, "E28.13.1", {"start": v(25.34, -22.17) * mm, "end": v(26.43, -22.38) * mm});
            skLineSegment(sketch, "E28.13.2", {"start": v(24.33, -21.97) * mm, "end": v(25.34, -22.17) * mm});
            skLineSegment(sketch, "E28.14.0", {"start": v(26.27, -17.29) * mm, "end": v(28.04, -18.49) * mm});
            skLineSegment(sketch, "E28.14.1", {"start": v(26.73, -19.4) * mm, "end": v(27.84, -19.32) * mm});
            skLineSegment(sketch, "E28.14.2", {"start": v(25.7, -19.47) * mm, "end": v(26.73, -19.4) * mm});
            skLineSegment(sketch, "E28.15.0", {"start": v(26.36, -14.44) * mm, "end": v(28.39, -15.14) * mm});
            skLineSegment(sketch, "E28.15.1", {"start": v(27.35, -16.36) * mm, "end": v(28.4, -16) * mm});
            skLineSegment(sketch, "E28.15.2", {"start": v(26.38, -16.7) * mm, "end": v(27.35, -16.36) * mm});
            skLineSegment(sketch, "E28.16.0", {"start": v(25.72, -11.67) * mm, "end": v(27.86, -11.82) * mm});
            skLineSegment(sketch, "E28.16.1", {"start": v(27.17, -13.26) * mm, "end": v(28.1, -12.64) * mm});
            skLineSegment(sketch, "E28.16.2", {"start": v(26.32, -13.84) * mm, "end": v(27.17, -13.26) * mm});
            skLineSegment(sketch, "E28.17.0", {"start": v(24.38, -9.15) * mm, "end": v(26.48, -8.74) * mm});
            skLineSegment(sketch, "E28.17.1", {"start": v(26.2, -10.31) * mm, "end": v(26.92, -9.48) * mm});
            skLineSegment(sketch, "E28.17.2", {"start": v(25.52, -11.1) * mm, "end": v(26.2, -10.31) * mm});
            skLineSegment(sketch, "E28.18.0", {"start": v(22.43, -7.07) * mm, "end": v(24.36, -6.13) * mm});
            skLineSegment(sketch, "E28.18.1", {"start": v(24.49, -7.72) * mm, "end": v(24.98, -6.72) * mm});
            skLineSegment(sketch, "E28.18.2", {"start": v(24.04, -8.65) * mm, "end": v(24.49, -7.72) * mm});
            skLineSegment(sketch, "E28.19.0", {"start": v(20.02, -5.56) * mm, "end": v(21.63, -4.16) * mm});
            skLineSegment(sketch, "E28.19.1", {"start": v(22.17, -5.66) * mm, "end": v(22.38, -4.57) * mm});
            skLineSegment(sketch, "E28.19.2", {"start": v(21.97, -6.67) * mm, "end": v(22.17, -5.66) * mm});
            skLineSegment(sketch, "E28.20.0", {"start": v(17.29, -4.73) * mm, "end": v(18.49, -2.96) * mm});
            skLineSegment(sketch, "E28.20.1", {"start": v(19.4, -4.27) * mm, "end": v(19.32, -3.16) * mm});
            skLineSegment(sketch, "E28.20.2", {"start": v(19.47, -5.3) * mm, "end": v(19.4, -4.27) * mm});
            skLineSegment(sketch, "E28.21.0", {"start": v(14.44, -4.64) * mm, "end": v(15.14, -2.61) * mm});
            skLineSegment(sketch, "E28.21.1", {"start": v(16.36, -3.65) * mm, "end": v(16, -2.6) * mm});
            skLineSegment(sketch, "E28.21.2", {"start": v(16.7, -4.62) * mm, "end": v(16.36, -3.65) * mm});
            skLineSegment(sketch, "E28.22.0", {"start": v(11.67, -5.28) * mm, "end": v(11.82, -3.14) * mm});
            skLineSegment(sketch, "E28.22.1", {"start": v(13.26, -3.83) * mm, "end": v(12.64, -2.9) * mm});
            skLineSegment(sketch, "E28.22.2", {"start": v(13.84, -4.68) * mm, "end": v(13.26, -3.83) * mm});
            skLineSegment(sketch, "E28.23.0", {"start": v(9.15, -6.62) * mm, "end": v(8.74, -4.52) * mm});
            skLineSegment(sketch, "E28.23.1", {"start": v(10.31, -4.8) * mm, "end": v(9.48, -4.08) * mm});
            skLineSegment(sketch, "E28.23.2", {"start": v(11.1, -5.48) * mm, "end": v(10.31, -4.8) * mm});
            skLineSegment(sketch, "E29.1.0", {"start": v(-22.33, -25.46) * mm, "end": v(-22.72, -26.5) * mm});
            skLineSegment(sketch, "E29.1.1", {"start": v(-21.96, -24.5) * mm, "end": v(-22.33, -25.46) * mm});
            skLineSegment(sketch, "E29.1.2", {"start": v(-20.22, -25.92) * mm, "end": v(-22.05, -27.04) * mm});
            skLineSegment(sketch, "E29.2.0", {"start": v(-19.88, -27.41) * mm, "end": v(-20.18, -28.49) * mm});
            skLineSegment(sketch, "E29.2.1", {"start": v(-19.61, -26.42) * mm, "end": v(-19.88, -27.41) * mm});
            skLineSegment(sketch, "E29.2.2", {"start": v(-17.74, -27.68) * mm, "end": v(-19.46, -28.95) * mm});
            skLineSegment(sketch, "E29.3.0", {"start": v(-17.27, -29.13) * mm, "end": v(-17.47, -30.23) * mm});
            skLineSegment(sketch, "E29.3.1", {"start": v(-17.09, -28.12) * mm, "end": v(-17.27, -29.13) * mm});
            skLineSegment(sketch, "E29.3.2", {"start": v(-15.11, -29.2) * mm, "end": v(-16.7, -30.63) * mm});
            skLineSegment(sketch, "E29.4.0", {"start": v(-14.5, -30.6) * mm, "end": v(-14.6, -31.7) * mm});
            skLineSegment(sketch, "E29.4.1", {"start": v(-14.42, -29.57) * mm, "end": v(-14.5, -30.6) * mm});
            skLineSegment(sketch, "E29.4.2", {"start": v(-12.36, -30.47) * mm, "end": v(-13.81, -32.04) * mm});
            skLineSegment(sketch, "E29.5.0", {"start": v(-11.62, -31.8) * mm, "end": v(-11.61, -32.92) * mm});
            skLineSegment(sketch, "E29.5.1", {"start": v(-11.63, -30.78) * mm, "end": v(-11.62, -31.8) * mm});
            skLineSegment(sketch, "E29.5.2", {"start": v(-9.5, -31.48) * mm, "end": v(-10.8, -33.18) * mm});
            skLineSegment(sketch, "E29.6.0", {"start": v(-8.64, -32.75) * mm, "end": v(-8.53, -33.85) * mm});
            skLineSegment(sketch, "E29.6.1", {"start": v(-8.74, -31.72) * mm, "end": v(-8.64, -32.75) * mm});
            skLineSegment(sketch, "E29.6.2", {"start": v(-6.55, -32.22) * mm, "end": v(-7.69, -34.03) * mm});
            skLineSegment(sketch, "E29.7.0", {"start": v(-5.58, -33.4) * mm, "end": v(-5.37, -34.5) * mm});
            skLineSegment(sketch, "E29.7.1", {"start": v(-5.78, -32.4) * mm, "end": v(-5.58, -33.4) * mm});
            skLineSegment(sketch, "E29.7.2", {"start": v(-3.55, -32.69) * mm, "end": v(-4.52, -34.6) * mm});
            skLineSegment(sketch, "E29.8.0", {"start": v(-2.47, -33.78) * mm, "end": v(-2.16, -34.84) * mm});
            skLineSegment(sketch, "E29.8.1", {"start": v(-2.76, -32.79) * mm, "end": v(-2.47, -33.78) * mm});
            skLineSegment(sketch, "E29.8.2", {"start": v(-0.52, -32.87) * mm, "end": v(-1.3, -34.86) * mm});
            skLineSegment(sketch, "E29.9.0", {"start": v(0.65, -33.86) * mm, "end": v(1.06, -34.9) * mm});
            skLineSegment(sketch, "E29.9.1", {"start": v(0.27, -32.9) * mm, "end": v(0.65, -33.86) * mm});
            skLineSegment(sketch, "E29.9.2", {"start": v(2.52, -32.78) * mm, "end": v(1.92, -34.84) * mm});
            skLineSegment(sketch, "E29.10.0", {"start": v(3.77, -33.65) * mm, "end": v(4.28, -34.65) * mm});
            skLineSegment(sketch, "E29.10.1", {"start": v(3.3, -32.74) * mm, "end": v(3.77, -33.65) * mm});
            skLineSegment(sketch, "E29.10.2", {"start": v(5.53, -32.4) * mm, "end": v(5.12, -34.51) * mm});
            skLineSegment(sketch, "E29.11.0", {"start": v(6.86, -33.16) * mm, "end": v(7.46, -34.1) * mm});
            skLineSegment(sketch, "E29.11.1", {"start": v(6.31, -32.3) * mm, "end": v(6.86, -33.16) * mm});
            skLineSegment(sketch, "E29.11.2", {"start": v(8.5, -31.76) * mm, "end": v(8.29, -33.9) * mm});
            skLineSegment(sketch, "E29.12.0", {"start": v(9.9, -32.39) * mm, "end": v(10.57, -33.27) * mm});
            skLineSegment(sketch, "E29.12.1", {"start": v(9.27, -31.57) * mm, "end": v(9.9, -32.39) * mm});
            skLineSegment(sketch, "E29.12.2", {"start": v(11.4, -30.84) * mm, "end": v(11.38, -32.98) * mm});
            skLineSegment(sketch, "E29.13.0", {"start": v(12.84, -31.34) * mm, "end": v(13.6, -32.15) * mm});
            skLineSegment(sketch, "E29.13.1", {"start": v(12.14, -30.58) * mm, "end": v(12.84, -31.34) * mm});
            skLineSegment(sketch, "E29.13.2", {"start": v(14.2, -29.66) * mm, "end": v(14.37, -31.8) * mm});
            skLineSegment(sketch, "E29.14.0", {"start": v(15.68, -30.02) * mm, "end": v(16.5, -30.76) * mm});
            skLineSegment(sketch, "E29.14.1", {"start": v(14.9, -29.33) * mm, "end": v(15.68, -30.02) * mm});
            skLineSegment(sketch, "E29.14.2", {"start": v(16.87, -28.22) * mm, "end": v(17.24, -30.33) * mm});
            skLineSegment(sketch, "E29.15.0", {"start": v(18.38, -28.44) * mm, "end": v(19.27, -29.1) * mm});
            skLineSegment(sketch, "E29.15.1", {"start": v(17.55, -27.83) * mm, "end": v(18.38, -28.44) * mm});
            skLineSegment(sketch, "E29.15.2", {"start": v(19.4, -26.54) * mm, "end": v(19.97, -28.6) * mm});
            skLineSegment(sketch, "E29.16.0", {"start": v(20.93, -26.63) * mm, "end": v(21.88, -27.2) * mm});
            skLineSegment(sketch, "E29.16.1", {"start": v(20.05, -26.1) * mm, "end": v(20.93, -26.63) * mm});
            skLineSegment(sketch, "E29.16.2", {"start": v(21.77, -24.64) * mm, "end": v(22.52, -26.64) * mm});
            skLineSegment(sketch, "E29.17.0", {"start": v(23.3, -24.58) * mm, "end": v(24.3, -25.07) * mm});
            skLineSegment(sketch, "E29.17.1", {"start": v(22.37, -24.13) * mm, "end": v(23.3, -24.58) * mm});
            skLineSegment(sketch, "E29.17.2", {"start": v(23.95, -22.53) * mm, "end": v(24.89, -24.45) * mm});
            skLineSegment(sketch, "E29.18.0", {"start": v(25.46, -22.33) * mm, "end": v(26.5, -22.72) * mm});
            skLineSegment(sketch, "E29.18.1", {"start": v(24.5, -21.96) * mm, "end": v(25.46, -22.33) * mm});
            skLineSegment(sketch, "E29.18.2", {"start": v(25.92, -20.22) * mm, "end": v(27.04, -22.05) * mm});
            skLineSegment(sketch, "E29.19.0", {"start": v(27.41, -19.88) * mm, "end": v(28.49, -20.18) * mm});
            skLineSegment(sketch, "E29.19.1", {"start": v(26.42, -19.61) * mm, "end": v(27.41, -19.88) * mm});
            skLineSegment(sketch, "E29.19.2", {"start": v(27.68, -17.74) * mm, "end": v(28.95, -19.46) * mm});
            skLineSegment(sketch, "E29.20.0", {"start": v(29.13, -17.27) * mm, "end": v(30.23, -17.47) * mm});
            skLineSegment(sketch, "E29.20.1", {"start": v(28.12, -17.09) * mm, "end": v(29.13, -17.27) * mm});
            skLineSegment(sketch, "E29.20.2", {"start": v(29.2, -15.11) * mm, "end": v(30.63, -16.7) * mm});
            skLineSegment(sketch, "E29.21.0", {"start": v(30.6, -14.5) * mm, "end": v(31.7, -14.6) * mm});
            skLineSegment(sketch, "E29.21.1", {"start": v(29.57, -14.42) * mm, "end": v(30.6, -14.5) * mm});
            skLineSegment(sketch, "E29.21.2", {"start": v(30.47, -12.36) * mm, "end": v(32.04, -13.81) * mm});
            skLineSegment(sketch, "E29.22.0", {"start": v(31.8, -11.62) * mm, "end": v(32.92, -11.61) * mm});
            skLineSegment(sketch, "E29.22.1", {"start": v(30.78, -11.63) * mm, "end": v(31.8, -11.62) * mm});
            skLineSegment(sketch, "E29.22.2", {"start": v(31.48, -9.5) * mm, "end": v(33.18, -10.8) * mm});
            skLineSegment(sketch, "E29.23.0", {"start": v(32.75, -8.64) * mm, "end": v(33.85, -8.53) * mm});
            skLineSegment(sketch, "E29.23.1", {"start": v(31.72, -8.74) * mm, "end": v(32.75, -8.64) * mm});
            skLineSegment(sketch, "E29.23.2", {"start": v(32.22, -6.55) * mm, "end": v(34.03, -7.69) * mm});
            skLineSegment(sketch, "E29.24.0", {"start": v(33.4, -5.58) * mm, "end": v(34.5, -5.37) * mm});
            skLineSegment(sketch, "E29.24.1", {"start": v(32.4, -5.78) * mm, "end": v(33.4, -5.58) * mm});
            skLineSegment(sketch, "E29.24.2", {"start": v(32.69, -3.55) * mm, "end": v(34.6, -4.52) * mm});
            skLineSegment(sketch, "E29.25.0", {"start": v(33.78, -2.47) * mm, "end": v(34.84, -2.16) * mm});
            skLineSegment(sketch, "E29.25.1", {"start": v(32.79, -2.76) * mm, "end": v(33.78, -2.47) * mm});
            skLineSegment(sketch, "E29.25.2", {"start": v(32.87, -0.52) * mm, "end": v(34.86, -1.3) * mm});
            skLineSegment(sketch, "E29.26.0", {"start": v(33.86, 0.65) * mm, "end": v(34.9, 1.06) * mm});
            skLineSegment(sketch, "E29.26.1", {"start": v(32.9, 0.27) * mm, "end": v(33.86, 0.65) * mm});
            skLineSegment(sketch, "E29.26.2", {"start": v(32.78, 2.52) * mm, "end": v(34.84, 1.92) * mm});
            skLineSegment(sketch, "E29.27.0", {"start": v(33.65, 3.77) * mm, "end": v(34.65, 4.28) * mm});
            skLineSegment(sketch, "E29.27.1", {"start": v(32.74, 3.3) * mm, "end": v(33.65, 3.77) * mm});
            skLineSegment(sketch, "E29.27.2", {"start": v(32.4, 5.53) * mm, "end": v(34.51, 5.12) * mm});
            skLineSegment(sketch, "E29.28.0", {"start": v(33.16, 6.86) * mm, "end": v(34.1, 7.46) * mm});
            skLineSegment(sketch, "E29.28.1", {"start": v(32.3, 6.31) * mm, "end": v(33.16, 6.86) * mm});
            skLineSegment(sketch, "E29.28.2", {"start": v(31.76, 8.5) * mm, "end": v(33.9, 8.29) * mm});
            skLineSegment(sketch, "E29.29.0", {"start": v(32.39, 9.9) * mm, "end": v(33.27, 10.57) * mm});
            skLineSegment(sketch, "E29.29.1", {"start": v(31.57, 9.27) * mm, "end": v(32.39, 9.9) * mm});
            skLineSegment(sketch, "E29.29.2", {"start": v(30.84, 11.4) * mm, "end": v(32.98, 11.38) * mm});
            skLineSegment(sketch, "E29.30.0", {"start": v(31.34, 12.84) * mm, "end": v(32.15, 13.6) * mm});
            skLineSegment(sketch, "E29.30.1", {"start": v(30.58, 12.14) * mm, "end": v(31.34, 12.84) * mm});
            skLineSegment(sketch, "E29.30.2", {"start": v(29.66, 14.2) * mm, "end": v(31.8, 14.37) * mm});
            skLineSegment(sketch, "E29.31.0", {"start": v(30.02, 15.68) * mm, "end": v(30.76, 16.5) * mm});
            skLineSegment(sketch, "E29.31.1", {"start": v(29.33, 14.9) * mm, "end": v(30.02, 15.68) * mm});
            skLineSegment(sketch, "E29.31.2", {"start": v(28.22, 16.87) * mm, "end": v(30.33, 17.24) * mm});
            skLineSegment(sketch, "E29.32.0", {"start": v(28.44, 18.38) * mm, "end": v(29.1, 19.27) * mm});
            skLineSegment(sketch, "E29.32.1", {"start": v(27.83, 17.55) * mm, "end": v(28.44, 18.38) * mm});
            skLineSegment(sketch, "E29.32.2", {"start": v(26.54, 19.4) * mm, "end": v(28.6, 19.97) * mm});
            skLineSegment(sketch, "E29.33.0", {"start": v(26.63, 20.93) * mm, "end": v(27.2, 21.88) * mm});
            skLineSegment(sketch, "E29.33.1", {"start": v(26.1, 20.05) * mm, "end": v(26.63, 20.93) * mm});
            skLineSegment(sketch, "E29.33.2", {"start": v(24.64, 21.77) * mm, "end": v(26.64, 22.52) * mm});
            skLineSegment(sketch, "E29.34.0", {"start": v(24.58, 23.3) * mm, "end": v(25.07, 24.3) * mm});
            skLineSegment(sketch, "E29.34.1", {"start": v(24.13, 22.37) * mm, "end": v(24.58, 23.3) * mm});
            skLineSegment(sketch, "E29.34.2", {"start": v(22.53, 23.95) * mm, "end": v(24.45, 24.89) * mm});
            skLineSegment(sketch, "E29.35.0", {"start": v(22.33, 25.46) * mm, "end": v(22.72, 26.5) * mm});
            skLineSegment(sketch, "E29.35.1", {"start": v(21.96, 24.5) * mm, "end": v(22.33, 25.46) * mm});
            skLineSegment(sketch, "E29.35.2", {"start": v(20.22, 25.92) * mm, "end": v(22.05, 27.04) * mm});
            skLineSegment(sketch, "E29.36.0", {"start": v(19.88, 27.41) * mm, "end": v(20.18, 28.49) * mm});
            skLineSegment(sketch, "E29.36.1", {"start": v(19.61, 26.42) * mm, "end": v(19.88, 27.41) * mm});
            skLineSegment(sketch, "E29.36.2", {"start": v(17.74, 27.68) * mm, "end": v(19.46, 28.95) * mm});
            skLineSegment(sketch, "E29.37.0", {"start": v(17.27, 29.13) * mm, "end": v(17.47, 30.23) * mm});
            skLineSegment(sketch, "E29.37.1", {"start": v(17.09, 28.12) * mm, "end": v(17.27, 29.13) * mm});
            skLineSegment(sketch, "E29.37.2", {"start": v(15.11, 29.2) * mm, "end": v(16.7, 30.63) * mm});
            skLineSegment(sketch, "E29.38.0", {"start": v(14.5, 30.6) * mm, "end": v(14.6, 31.7) * mm});
            skLineSegment(sketch, "E29.38.1", {"start": v(14.42, 29.57) * mm, "end": v(14.5, 30.6) * mm});
            skLineSegment(sketch, "E29.38.2", {"start": v(12.36, 30.47) * mm, "end": v(13.81, 32.04) * mm});
            skLineSegment(sketch, "E29.39.0", {"start": v(11.62, 31.8) * mm, "end": v(11.61, 32.92) * mm});
            skLineSegment(sketch, "E29.39.1", {"start": v(11.63, 30.78) * mm, "end": v(11.62, 31.8) * mm});
            skLineSegment(sketch, "E29.39.2", {"start": v(9.5, 31.48) * mm, "end": v(10.8, 33.18) * mm});
            skLineSegment(sketch, "E29.40.0", {"start": v(8.64, 32.75) * mm, "end": v(8.53, 33.85) * mm});
            skLineSegment(sketch, "E29.40.1", {"start": v(8.74, 31.72) * mm, "end": v(8.64, 32.75) * mm});
            skLineSegment(sketch, "E29.40.2", {"start": v(6.55, 32.22) * mm, "end": v(7.69, 34.03) * mm});
            skLineSegment(sketch, "E29.41.0", {"start": v(5.58, 33.4) * mm, "end": v(5.37, 34.5) * mm});
            skLineSegment(sketch, "E29.41.1", {"start": v(5.78, 32.4) * mm, "end": v(5.58, 33.4) * mm});
            skLineSegment(sketch, "E29.41.2", {"start": v(3.55, 32.69) * mm, "end": v(4.52, 34.6) * mm});
            skLineSegment(sketch, "E29.42.0", {"start": v(2.47, 33.78) * mm, "end": v(2.16, 34.84) * mm});
            skLineSegment(sketch, "E29.42.1", {"start": v(2.76, 32.79) * mm, "end": v(2.47, 33.78) * mm});
            skLineSegment(sketch, "E29.42.2", {"start": v(0.52, 32.87) * mm, "end": v(1.3, 34.86) * mm});
            skLineSegment(sketch, "E29.43.0", {"start": v(-0.65, 33.86) * mm, "end": v(-1.06, 34.9) * mm});
            skLineSegment(sketch, "E29.43.1", {"start": v(-0.27, 32.9) * mm, "end": v(-0.65, 33.86) * mm});
            skLineSegment(sketch, "E29.43.2", {"start": v(-2.52, 32.78) * mm, "end": v(-1.92, 34.84) * mm});
            skLineSegment(sketch, "E29.44.0", {"start": v(-3.77, 33.65) * mm, "end": v(-4.28, 34.65) * mm});
            skLineSegment(sketch, "E29.44.1", {"start": v(-3.3, 32.74) * mm, "end": v(-3.77, 33.65) * mm});
            skLineSegment(sketch, "E29.44.2", {"start": v(-5.53, 32.4) * mm, "end": v(-5.12, 34.51) * mm});
            skLineSegment(sketch, "E29.45.0", {"start": v(-6.86, 33.16) * mm, "end": v(-7.46, 34.1) * mm});
            skLineSegment(sketch, "E29.45.1", {"start": v(-6.31, 32.3) * mm, "end": v(-6.86, 33.16) * mm});
            skLineSegment(sketch, "E29.45.2", {"start": v(-8.5, 31.76) * mm, "end": v(-8.29, 33.9) * mm});
            skLineSegment(sketch, "E29.46.0", {"start": v(-9.9, 32.39) * mm, "end": v(-10.57, 33.27) * mm});
            skLineSegment(sketch, "E29.46.1", {"start": v(-9.27, 31.57) * mm, "end": v(-9.9, 32.39) * mm});
            skLineSegment(sketch, "E29.46.2", {"start": v(-11.4, 30.84) * mm, "end": v(-11.38, 32.98) * mm});
            skLineSegment(sketch, "E29.47.0", {"start": v(-12.84, 31.34) * mm, "end": v(-13.6, 32.15) * mm});
            skLineSegment(sketch, "E29.47.1", {"start": v(-12.14, 30.58) * mm, "end": v(-12.84, 31.34) * mm});
            skLineSegment(sketch, "E29.47.2", {"start": v(-14.2, 29.66) * mm, "end": v(-14.37, 31.8) * mm});
            skLineSegment(sketch, "E29.48.0", {"start": v(-15.68, 30.02) * mm, "end": v(-16.5, 30.76) * mm});
            skLineSegment(sketch, "E29.48.1", {"start": v(-14.9, 29.33) * mm, "end": v(-15.68, 30.02) * mm});
            skLineSegment(sketch, "E29.48.2", {"start": v(-16.87, 28.22) * mm, "end": v(-17.24, 30.33) * mm});
            skLineSegment(sketch, "E29.49.0", {"start": v(-18.38, 28.44) * mm, "end": v(-19.27, 29.1) * mm});
            skLineSegment(sketch, "E29.49.1", {"start": v(-17.55, 27.83) * mm, "end": v(-18.38, 28.44) * mm});
            skLineSegment(sketch, "E29.49.2", {"start": v(-19.4, 26.54) * mm, "end": v(-19.97, 28.6) * mm});
            skLineSegment(sketch, "E29.50.0", {"start": v(-20.93, 26.63) * mm, "end": v(-21.88, 27.2) * mm});
            skLineSegment(sketch, "E29.50.1", {"start": v(-20.05, 26.1) * mm, "end": v(-20.93, 26.63) * mm});
            skLineSegment(sketch, "E29.50.2", {"start": v(-21.77, 24.64) * mm, "end": v(-22.52, 26.64) * mm});
            skLineSegment(sketch, "E29.51.0", {"start": v(-23.3, 24.58) * mm, "end": v(-24.3, 25.07) * mm});
            skLineSegment(sketch, "E29.51.1", {"start": v(-22.37, 24.13) * mm, "end": v(-23.3, 24.58) * mm});
            skLineSegment(sketch, "E29.51.2", {"start": v(-23.95, 22.53) * mm, "end": v(-24.89, 24.45) * mm});
            skLineSegment(sketch, "E29.52.0", {"start": v(-25.46, 22.33) * mm, "end": v(-26.5, 22.72) * mm});
            skLineSegment(sketch, "E29.52.1", {"start": v(-24.5, 21.96) * mm, "end": v(-25.46, 22.33) * mm});
            skLineSegment(sketch, "E29.52.2", {"start": v(-25.92, 20.22) * mm, "end": v(-27.04, 22.05) * mm});
            skLineSegment(sketch, "E29.53.0", {"start": v(-27.41, 19.88) * mm, "end": v(-28.49, 20.18) * mm});
            skLineSegment(sketch, "E29.53.1", {"start": v(-26.42, 19.61) * mm, "end": v(-27.41, 19.88) * mm});
            skLineSegment(sketch, "E29.53.2", {"start": v(-27.68, 17.74) * mm, "end": v(-28.95, 19.46) * mm});
            skLineSegment(sketch, "E29.54.0", {"start": v(-29.13, 17.27) * mm, "end": v(-30.23, 17.47) * mm});
            skLineSegment(sketch, "E29.54.1", {"start": v(-28.12, 17.09) * mm, "end": v(-29.13, 17.27) * mm});
            skLineSegment(sketch, "E29.54.2", {"start": v(-29.2, 15.11) * mm, "end": v(-30.63, 16.7) * mm});
            skLineSegment(sketch, "E29.55.0", {"start": v(-30.6, 14.5) * mm, "end": v(-31.7, 14.6) * mm});
            skLineSegment(sketch, "E29.55.1", {"start": v(-29.57, 14.42) * mm, "end": v(-30.6, 14.5) * mm});
            skLineSegment(sketch, "E29.55.2", {"start": v(-30.47, 12.36) * mm, "end": v(-32.04, 13.81) * mm});
            skLineSegment(sketch, "E29.56.0", {"start": v(-31.8, 11.62) * mm, "end": v(-32.92, 11.61) * mm});
            skLineSegment(sketch, "E29.56.1", {"start": v(-30.78, 11.63) * mm, "end": v(-31.8, 11.62) * mm});
            skLineSegment(sketch, "E29.56.2", {"start": v(-31.48, 9.5) * mm, "end": v(-33.18, 10.8) * mm});
            skLineSegment(sketch, "E29.57.0", {"start": v(-32.75, 8.64) * mm, "end": v(-33.85, 8.53) * mm});
            skLineSegment(sketch, "E29.57.1", {"start": v(-31.72, 8.74) * mm, "end": v(-32.75, 8.64) * mm});
            skLineSegment(sketch, "E29.57.2", {"start": v(-32.22, 6.55) * mm, "end": v(-34.03, 7.69) * mm});
            skLineSegment(sketch, "E29.58.0", {"start": v(-33.4, 5.58) * mm, "end": v(-34.5, 5.37) * mm});
            skLineSegment(sketch, "E29.58.1", {"start": v(-32.4, 5.78) * mm, "end": v(-33.4, 5.58) * mm});
            skLineSegment(sketch, "E29.58.2", {"start": v(-32.69, 3.55) * mm, "end": v(-34.6, 4.52) * mm});
            skLineSegment(sketch, "E29.59.0", {"start": v(-33.78, 2.47) * mm, "end": v(-34.84, 2.16) * mm});
            skLineSegment(sketch, "E29.59.1", {"start": v(-32.79, 2.76) * mm, "end": v(-33.78, 2.47) * mm});
            skLineSegment(sketch, "E29.59.2", {"start": v(-32.87, 0.52) * mm, "end": v(-34.86, 1.3) * mm});
            skLineSegment(sketch, "E29.60.0", {"start": v(-33.86, -0.65) * mm, "end": v(-34.9, -1.06) * mm});
            skLineSegment(sketch, "E29.60.1", {"start": v(-32.9, -0.27) * mm, "end": v(-33.86, -0.65) * mm});
            skLineSegment(sketch, "E29.60.2", {"start": v(-32.78, -2.52) * mm, "end": v(-34.84, -1.92) * mm});
            skLineSegment(sketch, "E29.61.0", {"start": v(-33.65, -3.77) * mm, "end": v(-34.65, -4.28) * mm});
            skLineSegment(sketch, "E29.61.1", {"start": v(-32.74, -3.3) * mm, "end": v(-33.65, -3.77) * mm});
            skLineSegment(sketch, "E29.61.2", {"start": v(-32.4, -5.53) * mm, "end": v(-34.51, -5.12) * mm});
            skLineSegment(sketch, "E29.62.0", {"start": v(-33.16, -6.86) * mm, "end": v(-34.1, -7.46) * mm});
            skLineSegment(sketch, "E29.62.1", {"start": v(-32.3, -6.31) * mm, "end": v(-33.16, -6.86) * mm});
            skLineSegment(sketch, "E29.62.2", {"start": v(-31.76, -8.5) * mm, "end": v(-33.9, -8.29) * mm});
            skLineSegment(sketch, "E29.63.0", {"start": v(-32.39, -9.9) * mm, "end": v(-33.27, -10.57) * mm});
            skLineSegment(sketch, "E29.63.1", {"start": v(-31.57, -9.27) * mm, "end": v(-32.39, -9.9) * mm});
            skLineSegment(sketch, "E29.63.2", {"start": v(-30.84, -11.4) * mm, "end": v(-32.98, -11.38) * mm});
            skLineSegment(sketch, "E29.64.0", {"start": v(-31.34, -12.84) * mm, "end": v(-32.15, -13.6) * mm});
            skLineSegment(sketch, "E29.64.1", {"start": v(-30.58, -12.14) * mm, "end": v(-31.34, -12.84) * mm});
            skLineSegment(sketch, "E29.64.2", {"start": v(-29.66, -14.2) * mm, "end": v(-31.8, -14.37) * mm});
            skLineSegment(sketch, "E29.65.0", {"start": v(-30.02, -15.68) * mm, "end": v(-30.76, -16.5) * mm});
            skLineSegment(sketch, "E29.65.1", {"start": v(-29.33, -14.9) * mm, "end": v(-30.02, -15.68) * mm});
            skLineSegment(sketch, "E29.65.2", {"start": v(-28.22, -16.87) * mm, "end": v(-30.33, -17.24) * mm});
            skLineSegment(sketch, "E29.66.0", {"start": v(-28.44, -18.38) * mm, "end": v(-29.1, -19.27) * mm});
            skLineSegment(sketch, "E29.66.1", {"start": v(-27.83, -17.55) * mm, "end": v(-28.44, -18.38) * mm});
            skLineSegment(sketch, "E29.66.2", {"start": v(-26.54, -19.4) * mm, "end": v(-28.6, -19.97) * mm});
            skLineSegment(sketch, "E29.67.0", {"start": v(-26.63, -20.93) * mm, "end": v(-27.2, -21.88) * mm});
            skLineSegment(sketch, "E29.67.1", {"start": v(-26.1, -20.05) * mm, "end": v(-26.63, -20.93) * mm});
            skLineSegment(sketch, "E29.67.2", {"start": v(-24.64, -21.77) * mm, "end": v(-26.64, -22.52) * mm});
            skCircle(sketch, "E30", {"center": v(-44.91, -72.78) * mm, "radius": 10 * mm, "construction": true});
            skCircle(sketch, "E31", {"center": v(0, -58.38) * mm, "radius": 11.92 * mm, "construction": true});
            skArc(sketch, "E32", {"start": v(-44.62, -61.79) * mm, "mid": v(-44.91, -61.78) * mm, "end": v(-45.2, -61.79) * mm});
            skCircle(sketch, "E33", {"center": v(-44.91, -72.78) * mm, "radius": 2.75 * mm});
            skLineSegment(sketch, "E34", {"start": v(-45.7, -72.78) * mm, "end": v(-45.7, -61.81) * mm, "construction": true});
            skLineSegment(sketch, "E35", {"start": v(-44.13, -72.78) * mm, "end": v(-44.13, -61.81) * mm, "construction": true});
            skLineSegment(sketch, "E36", {"start": v(-44.13, -62.81) * mm, "end": v(-43.94, -63.9) * mm});
            skLineSegment(sketch, "E37", {"start": v(-43.94, -63.9) * mm, "end": v(-44.3, -61.8) * mm});
            skLineSegment(sketch, "E38", {"start": v(-44.91, -72.78) * mm, "end": v(-44.91, -58.89) * mm, "construction": true});
            skLineSegment(sketch, "E39.MirrorCS", {"start": v(-45.9, -63.9) * mm, "end": v(-45.52, -61.8) * mm});
            skPoint(sketch, "E40", {"position": v(-44.62, -61.79) * mm});
            skPoint(sketch, "E41", {"position": v(-44.17, -62.6) * mm});
            skArc(sketch, "E42.MirrorCS", {"start": v(-45.66, -62.6) * mm, "mid": v(-45.48, -62.17) * mm, "end": v(-45.2, -61.79) * mm});
            skArc(sketch, "E43.1.0", {"start": v(-48.8, -63.13) * mm, "mid": v(-48.77, -62.78) * mm, "end": v(-48.66, -62.44) * mm});
            skArc(sketch, "E43.1.1", {"start": v(-47.45, -62.69) * mm, "mid": v(-47.67, -62.42) * mm, "end": v(-47.96, -62.21) * mm});
            skLineSegment(sketch, "E43.1.2", {"start": v(-48.59, -64.65) * mm, "end": v(-48.89, -62.52) * mm});
            skLineSegment(sketch, "E43.1.3", {"start": v(-46.73, -64.04) * mm, "end": v(-47.73, -62.15) * mm});
            skArc(sketch, "E43.2.0", {"start": v(-51.6, -64.8) * mm, "mid": v(-51.68, -64.46) * mm, "end": v(-51.68, -64.1) * mm});
            skArc(sketch, "E43.2.1", {"start": v(-50.44, -63.96) * mm, "mid": v(-50.74, -63.78) * mm, "end": v(-51.08, -63.67) * mm});
            skLineSegment(sketch, "E43.2.2", {"start": v(-50.92, -66.18) * mm, "end": v(-51.86, -64.25) * mm});
            skLineSegment(sketch, "E43.2.3", {"start": v(-49.34, -65.03) * mm, "end": v(-50.88, -63.54) * mm});
            skArc(sketch, "E43.3.0", {"start": v(-53.73, -67.26) * mm, "mid": v(-53.92, -66.96) * mm, "end": v(-54.03, -66.62) * mm});
            skArc(sketch, "E43.3.1", {"start": v(-52.9, -66.1) * mm, "mid": v(-53.24, -66.02) * mm, "end": v(-53.6, -66.02) * mm});
            skLineSegment(sketch, "E43.3.2", {"start": v(-52.67, -68.36) * mm, "end": v(-54.16, -66.82) * mm});
            skLineSegment(sketch, "E43.3.3", {"start": v(-51.52, -66.78) * mm, "end": v(-53.44, -65.84) * mm});
            skArc(sketch, "E43.4.0", {"start": v(-55, -70.25) * mm, "mid": v(-55.28, -70.02) * mm, "end": v(-55.48, -69.74) * mm});
            skArc(sketch, "E43.4.1", {"start": v(-54.57, -68.9) * mm, "mid": v(-54.92, -68.92) * mm, "end": v(-55.26, -69.03) * mm});
            skLineSegment(sketch, "E43.4.2", {"start": v(-53.66, -70.97) * mm, "end": v(-55.55, -69.97) * mm});
            skLineSegment(sketch, "E43.4.3", {"start": v(-53.05, -69.11) * mm, "end": v(-55.17, -68.81) * mm});
            skArc(sketch, "E43.5.0", {"start": v(-55.3, -73.5) * mm, "mid": v(-55.62, -73.36) * mm, "end": v(-55.9, -73.15) * mm});
            skArc(sketch, "E43.5.1", {"start": v(-55.3, -72.07) * mm, "mid": v(-55.62, -72.2) * mm, "end": v(-55.9, -72.41) * mm});
            skLineSegment(sketch, "E43.5.2", {"start": v(-53.79, -73.76) * mm, "end": v(-55.9, -73.39) * mm});
            skLineSegment(sketch, "E43.5.3", {"start": v(-53.79, -71.8) * mm, "end": v(-55.9, -72.18) * mm});
            skArc(sketch, "E43.6.0", {"start": v(-54.57, -76.67) * mm, "mid": v(-54.92, -76.64) * mm, "end": v(-55.26, -76.53) * mm});
            skArc(sketch, "E43.6.1", {"start": v(-55, -75.31) * mm, "mid": v(-55.28, -75.54) * mm, "end": v(-55.48, -75.83) * mm});
            skLineSegment(sketch, "E43.6.2", {"start": v(-53.05, -76.46) * mm, "end": v(-55.17, -76.75) * mm});
            skLineSegment(sketch, "E43.6.3", {"start": v(-53.66, -74.6) * mm, "end": v(-55.55, -75.6) * mm});
            skArc(sketch, "E43.7.0", {"start": v(-52.9, -79.46) * mm, "mid": v(-53.24, -79.54) * mm, "end": v(-53.6, -79.55) * mm});
            skArc(sketch, "E43.7.1", {"start": v(-53.73, -78.3) * mm, "mid": v(-53.92, -78.6) * mm, "end": v(-54.03, -78.94) * mm});
            skLineSegment(sketch, "E43.7.2", {"start": v(-51.52, -78.8) * mm, "end": v(-53.44, -79.73) * mm});
            skLineSegment(sketch, "E43.7.3", {"start": v(-52.67, -77.2) * mm, "end": v(-54.16, -78.75) * mm});
            skArc(sketch, "E43.8.0", {"start": v(-50.44, -81.6) * mm, "mid": v(-50.74, -81.79) * mm, "end": v(-51.08, -81.9) * mm});
            skArc(sketch, "E43.8.1", {"start": v(-51.6, -80.76) * mm, "mid": v(-51.68, -81.1) * mm, "end": v(-51.68, -81.46) * mm});
            skLineSegment(sketch, "E43.8.2", {"start": v(-49.34, -80.54) * mm, "end": v(-50.88, -82.03) * mm});
            skLineSegment(sketch, "E43.8.3", {"start": v(-50.92, -79.39) * mm, "end": v(-51.86, -81.31) * mm});
            skArc(sketch, "E43.9.0", {"start": v(-47.45, -82.88) * mm, "mid": v(-47.67, -83.15) * mm, "end": v(-47.96, -83.35) * mm});
            skArc(sketch, "E43.9.1", {"start": v(-48.8, -82.44) * mm, "mid": v(-48.77, -82.79) * mm, "end": v(-48.66, -83.12) * mm});
            skLineSegment(sketch, "E43.9.2", {"start": v(-46.73, -81.52) * mm, "end": v(-47.73, -83.42) * mm});
            skLineSegment(sketch, "E43.9.3", {"start": v(-48.59, -80.92) * mm, "end": v(-48.89, -83.04) * mm});
            skArc(sketch, "E43.10.0", {"start": v(-44.2, -83.17) * mm, "mid": v(-44.34, -83.5) * mm, "end": v(-44.54, -83.78) * mm});
            skArc(sketch, "E43.10.1", {"start": v(-45.63, -83.17) * mm, "mid": v(-45.5, -83.5) * mm, "end": v(-45.29, -83.78) * mm});
            skLineSegment(sketch, "E43.10.2", {"start": v(-43.94, -81.66) * mm, "end": v(-44.3, -83.77) * mm});
            skLineSegment(sketch, "E43.10.3", {"start": v(-45.9, -81.66) * mm, "end": v(-45.52, -83.77) * mm});
            skArc(sketch, "E43.11.0", {"start": v(-41.03, -82.44) * mm, "mid": v(-41.06, -82.79) * mm, "end": v(-41.16, -83.12) * mm});
            skArc(sketch, "E43.11.1", {"start": v(-42.38, -82.88) * mm, "mid": v(-42.15, -83.15) * mm, "end": v(-41.87, -83.35) * mm});
            skLineSegment(sketch, "E43.11.2", {"start": v(-41.24, -80.92) * mm, "end": v(-40.94, -83.04) * mm});
            skLineSegment(sketch, "E43.11.3", {"start": v(-43.1, -81.52) * mm, "end": v(-42.1, -83.42) * mm});
            skArc(sketch, "E43.12.0", {"start": v(-38.23, -80.76) * mm, "mid": v(-38.15, -81.1) * mm, "end": v(-38.15, -81.46) * mm});
            skArc(sketch, "E43.12.1", {"start": v(-39.39, -81.6) * mm, "mid": v(-39.09, -81.79) * mm, "end": v(-38.75, -81.9) * mm});
            skLineSegment(sketch, "E43.12.2", {"start": v(-38.9, -79.39) * mm, "end": v(-37.97, -81.31) * mm});
            skLineSegment(sketch, "E43.12.3", {"start": v(-40.49, -80.54) * mm, "end": v(-38.95, -82.03) * mm});
            skArc(sketch, "E43.13.0", {"start": v(-36.1, -78.3) * mm, "mid": v(-35.91, -78.6) * mm, "end": v(-35.8, -78.94) * mm});
            skArc(sketch, "E43.13.1", {"start": v(-36.93, -79.46) * mm, "mid": v(-36.6, -79.54) * mm, "end": v(-36.24, -79.55) * mm});
            skLineSegment(sketch, "E43.13.2", {"start": v(-37.16, -77.2) * mm, "end": v(-35.67, -78.75) * mm});
            skLineSegment(sketch, "E43.13.3", {"start": v(-38.31, -78.8) * mm, "end": v(-36.38, -79.73) * mm});
            skArc(sketch, "E43.14.0", {"start": v(-34.82, -75.31) * mm, "mid": v(-34.55, -75.54) * mm, "end": v(-34.34, -75.83) * mm});
            skArc(sketch, "E43.14.1", {"start": v(-35.26, -76.67) * mm, "mid": v(-34.9, -76.64) * mm, "end": v(-34.57, -76.53) * mm});
            skLineSegment(sketch, "E43.14.2", {"start": v(-36.17, -74.6) * mm, "end": v(-34.28, -75.6) * mm});
            skLineSegment(sketch, "E43.14.3", {"start": v(-36.78, -76.46) * mm, "end": v(-34.66, -76.75) * mm});
            skArc(sketch, "E43.15.0", {"start": v(-34.53, -72.07) * mm, "mid": v(-34.2, -72.2) * mm, "end": v(-33.92, -72.41) * mm});
            skArc(sketch, "E43.15.1", {"start": v(-34.53, -73.5) * mm, "mid": v(-34.2, -73.36) * mm, "end": v(-33.92, -73.15) * mm});
            skLineSegment(sketch, "E43.15.2", {"start": v(-36.04, -71.8) * mm, "end": v(-33.93, -72.18) * mm});
            skLineSegment(sketch, "E43.15.3", {"start": v(-36.04, -73.76) * mm, "end": v(-33.93, -73.39) * mm});
            skArc(sketch, "E43.16.0", {"start": v(-35.26, -68.9) * mm, "mid": v(-34.9, -68.92) * mm, "end": v(-34.57, -69.03) * mm});
            skArc(sketch, "E43.16.1", {"start": v(-34.82, -70.25) * mm, "mid": v(-34.55, -70.02) * mm, "end": v(-34.34, -69.74) * mm});
            skLineSegment(sketch, "E43.16.2", {"start": v(-36.78, -69.11) * mm, "end": v(-34.66, -68.81) * mm});
            skLineSegment(sketch, "E43.16.3", {"start": v(-36.17, -70.97) * mm, "end": v(-34.28, -69.97) * mm});
            skArc(sketch, "E43.17.0", {"start": v(-36.93, -66.1) * mm, "mid": v(-36.6, -66.02) * mm, "end": v(-36.24, -66.02) * mm});
            skArc(sketch, "E43.17.1", {"start": v(-36.1, -67.26) * mm, "mid": v(-35.91, -66.96) * mm, "end": v(-35.8, -66.62) * mm});
            skLineSegment(sketch, "E43.17.2", {"start": v(-38.31, -66.78) * mm, "end": v(-36.38, -65.84) * mm});
            skLineSegment(sketch, "E43.17.3", {"start": v(-37.16, -68.36) * mm, "end": v(-35.67, -66.82) * mm});
            skArc(sketch, "E43.18.0", {"start": v(-39.39, -63.96) * mm, "mid": v(-39.09, -63.78) * mm, "end": v(-38.75, -63.67) * mm});
            skArc(sketch, "E43.18.1", {"start": v(-38.23, -64.8) * mm, "mid": v(-38.15, -64.46) * mm, "end": v(-38.15, -64.1) * mm});
            skLineSegment(sketch, "E43.18.2", {"start": v(-40.49, -65.03) * mm, "end": v(-38.95, -63.54) * mm});
            skLineSegment(sketch, "E43.18.3", {"start": v(-38.9, -66.18) * mm, "end": v(-37.97, -64.25) * mm});
            skArc(sketch, "E43.19.0", {"start": v(-42.38, -62.69) * mm, "mid": v(-42.15, -62.42) * mm, "end": v(-41.87, -62.21) * mm});
            skArc(sketch, "E43.19.1", {"start": v(-41.03, -63.13) * mm, "mid": v(-41.06, -62.78) * mm, "end": v(-41.16, -62.44) * mm});
            skLineSegment(sketch, "E43.19.2", {"start": v(-43.1, -64.04) * mm, "end": v(-42.1, -62.15) * mm});
            skLineSegment(sketch, "E43.19.3", {"start": v(-41.24, -64.65) * mm, "end": v(-40.94, -62.52) * mm});
            skArc(sketch, "E44.1.0", {"start": v(-48.03, -62.23) * mm, "mid": v(-48.31, -62.32) * mm, "end": v(-48.6, -62.42) * mm});
            skArc(sketch, "E44.2.0", {"start": v(-51.14, -63.71) * mm, "mid": v(-51.38, -63.88) * mm, "end": v(-51.61, -64.06) * mm});
            skArc(sketch, "E44.3.0", {"start": v(-53.64, -66.08) * mm, "mid": v(-53.81, -66.32) * mm, "end": v(-53.98, -66.56) * mm});
            skArc(sketch, "E44.4.0", {"start": v(-55.28, -69.1) * mm, "mid": v(-55.38, -69.38) * mm, "end": v(-55.46, -69.66) * mm});
            skArc(sketch, "E44.5.0", {"start": v(-55.91, -72.5) * mm, "mid": v(-55.91, -72.78) * mm, "end": v(-55.91, -73.08) * mm});
            skArc(sketch, "E44.6.0", {"start": v(-55.46, -75.9) * mm, "mid": v(-55.38, -76.18) * mm, "end": v(-55.28, -76.46) * mm});
            skArc(sketch, "E44.7.0", {"start": v(-53.98, -79) * mm, "mid": v(-53.81, -79.25) * mm, "end": v(-53.64, -79.48) * mm});
            skArc(sketch, "E44.8.0", {"start": v(-51.61, -81.5) * mm, "mid": v(-51.38, -81.68) * mm, "end": v(-51.14, -81.85) * mm});
            skArc(sketch, "E44.9.0", {"start": v(-48.6, -83.15) * mm, "mid": v(-48.31, -83.24) * mm, "end": v(-48.03, -83.33) * mm});
            skArc(sketch, "E44.10.0", {"start": v(-45.2, -83.78) * mm, "mid": v(-44.91, -83.78) * mm, "end": v(-44.62, -83.78) * mm});
            skArc(sketch, "E44.11.0", {"start": v(-41.8, -83.33) * mm, "mid": v(-41.51, -83.24) * mm, "end": v(-41.24, -83.15) * mm});
            skArc(sketch, "E44.12.0", {"start": v(-38.69, -81.85) * mm, "mid": v(-38.45, -81.68) * mm, "end": v(-38.21, -81.5) * mm});
            skArc(sketch, "E44.13.0", {"start": v(-36.2, -79.48) * mm, "mid": v(-36.01, -79.25) * mm, "end": v(-35.85, -79) * mm});
            skArc(sketch, "E44.14.0", {"start": v(-34.55, -76.46) * mm, "mid": v(-34.45, -76.18) * mm, "end": v(-34.37, -75.9) * mm});
            skArc(sketch, "E44.15.0", {"start": v(-33.92, -73.08) * mm, "mid": v(-33.91, -72.78) * mm, "end": v(-33.92, -72.5) * mm});
            skArc(sketch, "E44.16.0", {"start": v(-34.37, -69.66) * mm, "mid": v(-34.45, -69.38) * mm, "end": v(-34.55, -69.1) * mm});
            skArc(sketch, "E44.17.0", {"start": v(-35.85, -66.56) * mm, "mid": v(-36.01, -66.32) * mm, "end": v(-36.2, -66.08) * mm});
            skArc(sketch, "E44.18.0", {"start": v(-38.21, -64.06) * mm, "mid": v(-38.45, -63.88) * mm, "end": v(-38.69, -63.71) * mm});
            skArc(sketch, "E44.19.0", {"start": v(-41.24, -62.42) * mm, "mid": v(-41.51, -62.32) * mm, "end": v(-41.8, -62.23) * mm});
            skArc(sketch, "E45", {"start": v(-43.94, -63.9) * mm, "mid": v(-43.52, -63.97) * mm, "end": v(-43.1, -64.04) * mm});
            skArc(sketch, "E46.1.0", {"start": v(-46.73, -64.04) * mm, "mid": v(-46.31, -63.97) * mm, "end": v(-45.9, -63.9) * mm});
            skArc(sketch, "E46.2.0", {"start": v(-49.34, -65.03) * mm, "mid": v(-48.97, -64.83) * mm, "end": v(-48.59, -64.65) * mm});
            skArc(sketch, "E46.3.0", {"start": v(-51.52, -66.78) * mm, "mid": v(-51.23, -66.47) * mm, "end": v(-50.92, -66.18) * mm});
            skArc(sketch, "E46.4.0", {"start": v(-53.05, -69.11) * mm, "mid": v(-52.87, -68.73) * mm, "end": v(-52.67, -68.36) * mm});
            skArc(sketch, "E46.5.0", {"start": v(-53.79, -71.8) * mm, "mid": v(-53.73, -71.39) * mm, "end": v(-53.66, -70.97) * mm});
            skArc(sketch, "E46.6.0", {"start": v(-53.66, -74.6) * mm, "mid": v(-53.73, -74.18) * mm, "end": v(-53.79, -73.76) * mm});
            skArc(sketch, "E46.7.0", {"start": v(-52.67, -77.2) * mm, "mid": v(-52.87, -76.84) * mm, "end": v(-53.05, -76.46) * mm});
            skArc(sketch, "E46.8.0", {"start": v(-50.92, -79.39) * mm, "mid": v(-51.23, -79.1) * mm, "end": v(-51.52, -78.8) * mm});
            skArc(sketch, "E46.9.0", {"start": v(-48.59, -80.92) * mm, "mid": v(-48.97, -80.74) * mm, "end": v(-49.34, -80.54) * mm});
            skArc(sketch, "E46.10.0", {"start": v(-45.9, -81.66) * mm, "mid": v(-46.31, -81.6) * mm, "end": v(-46.73, -81.52) * mm});
            skArc(sketch, "E46.11.0", {"start": v(-43.1, -81.52) * mm, "mid": v(-43.52, -81.6) * mm, "end": v(-43.94, -81.66) * mm});
            skArc(sketch, "E46.12.0", {"start": v(-40.49, -80.54) * mm, "mid": v(-40.86, -80.74) * mm, "end": v(-41.24, -80.92) * mm});
            skArc(sketch, "E46.13.0", {"start": v(-38.31, -78.8) * mm, "mid": v(-38.6, -79.1) * mm, "end": v(-38.9, -79.39) * mm});
            skArc(sketch, "E46.14.0", {"start": v(-36.78, -76.46) * mm, "mid": v(-36.96, -76.84) * mm, "end": v(-37.16, -77.2) * mm});
            skArc(sketch, "E46.15.0", {"start": v(-36.04, -73.76) * mm, "mid": v(-36.1, -74.18) * mm, "end": v(-36.17, -74.6) * mm});
            skArc(sketch, "E46.16.0", {"start": v(-36.17, -70.97) * mm, "mid": v(-36.1, -71.39) * mm, "end": v(-36.04, -71.8) * mm});
            skArc(sketch, "E46.17.0", {"start": v(-37.16, -68.36) * mm, "mid": v(-36.96, -68.73) * mm, "end": v(-36.78, -69.11) * mm});
            skArc(sketch, "E46.18.0", {"start": v(-38.9, -66.18) * mm, "mid": v(-38.6, -66.47) * mm, "end": v(-38.31, -66.78) * mm});
            skArc(sketch, "E46.19.0", {"start": v(-41.24, -64.65) * mm, "mid": v(-40.86, -64.83) * mm, "end": v(-40.49, -65.03) * mm});
            skArc(sketch, "E47.MirrorCS", {"start": v(-44.17, -62.6) * mm, "mid": v(-44.35, -62.17) * mm, "end": v(-44.62, -61.79) * mm});
            skArc(sketch, "E48", {"start": v(0.3, -45.46) * mm, "mid": v(0, -45.46) * mm, "end": v(-0.3, -45.46) * mm});
            skLineSegment(sketch, "E49", {"start": v(0.77, -46.42) * mm, "end": v(0.96, -47.5) * mm});
            skPoint(sketch, "E50", {"position": v(0.79, -46.48) * mm});
            skPoint(sketch, "E51", {"position": v(0.3, -45.46) * mm});
            skPoint(sketch, "E52", {"position": v(0.77, -46.42) * mm});
            skArc(sketch, "E53", {"start": v(0.77, -46.42) * mm, "mid": v(0.57, -45.92) * mm, "end": v(0.3, -45.46) * mm});
            skArc(sketch, "E54.MirrorCS", {"start": v(-0.77, -46.42) * mm, "mid": v(-0.57, -45.92) * mm, "end": v(-0.3, -45.46) * mm});
            skLineSegment(sketch, "E55.MirrorCS", {"start": v(-0.77, -46.42) * mm, "end": v(-0.96, -47.5) * mm});
            skPoint(sketch, "E56.orphan", {"position": v(0.6, -45.47) * mm});
            skPoint(sketch, "E57.orphan", {"position": v(-0.6, -45.47) * mm});
            skLineSegment(sketch, "E58.1.0", {"start": v(-3.84, -47.03) * mm, "end": v(-3.75, -48.12) * mm});
            skArc(sketch, "E58.1.1", {"start": v(-3.84, -47.03) * mm, "mid": v(-3.77, -46.5) * mm, "end": v(-3.63, -45.97) * mm});
            skArc(sketch, "E58.1.2", {"start": v(-3.06, -45.82) * mm, "mid": v(-3.34, -45.9) * mm, "end": v(-3.63, -45.97) * mm});
            skArc(sketch, "E58.1.3", {"start": v(-2.35, -46.63) * mm, "mid": v(-2.68, -46.2) * mm, "end": v(-3.06, -45.82) * mm});
            skLineSegment(sketch, "E58.1.4", {"start": v(-2.35, -46.63) * mm, "end": v(-1.88, -47.62) * mm});
            skLineSegment(sketch, "E58.2.0", {"start": v(-6.65, -48.4) * mm, "end": v(-6.27, -49.44) * mm});
            skArc(sketch, "E58.2.1", {"start": v(-6.65, -48.4) * mm, "mid": v(-6.72, -47.87) * mm, "end": v(-6.71, -47.34) * mm});
            skArc(sketch, "E58.2.2", {"start": v(-6.2, -47.04) * mm, "mid": v(-6.46, -47.19) * mm, "end": v(-6.71, -47.34) * mm});
            skArc(sketch, "E58.2.3", {"start": v(-5.3, -47.63) * mm, "mid": v(-5.74, -47.3) * mm, "end": v(-6.2, -47.04) * mm});
            skLineSegment(sketch, "E58.2.4", {"start": v(-5.3, -47.63) * mm, "end": v(-4.6, -48.47) * mm});
            skLineSegment(sketch, "E58.3.0", {"start": v(-9, -50.47) * mm, "end": v(-8.37, -51.37) * mm});
            skArc(sketch, "E58.3.1", {"start": v(-9, -50.47) * mm, "mid": v(-9.2, -49.97) * mm, "end": v(-9.34, -49.45) * mm});
            skArc(sketch, "E58.3.2", {"start": v(-8.93, -49.03) * mm, "mid": v(-9.14, -49.24) * mm, "end": v(-9.34, -49.45) * mm});
            skArc(sketch, "E58.3.3", {"start": v(-7.9, -49.37) * mm, "mid": v(-8.4, -49.17) * mm, "end": v(-8.93, -49.03) * mm});
            skLineSegment(sketch, "E58.3.4", {"start": v(-7.9, -49.37) * mm, "end": v(-7, -50) * mm});
            skLineSegment(sketch, "E58.4.0", {"start": v(-10.74, -53.07) * mm, "end": v(-9.9, -53.77) * mm});
            skArc(sketch, "E58.4.1", {"start": v(-10.74, -53.07) * mm, "mid": v(-11.07, -52.64) * mm, "end": v(-11.33, -52.17) * mm});
            skArc(sketch, "E58.4.2", {"start": v(-11.04, -51.66) * mm, "mid": v(-11.19, -51.92) * mm, "end": v(-11.33, -52.17) * mm});
            skArc(sketch, "E58.4.3", {"start": v(-9.97, -51.73) * mm, "mid": v(-10.5, -51.66) * mm, "end": v(-11.04, -51.66) * mm});
            skLineSegment(sketch, "E58.4.4", {"start": v(-9.97, -51.73) * mm, "end": v(-8.94, -52.1) * mm});
            skLineSegment(sketch, "E58.5.0", {"start": v(-11.75, -56.03) * mm, "end": v(-10.76, -56.5) * mm});
            skArc(sketch, "E58.5.1", {"start": v(-11.75, -56.03) * mm, "mid": v(-12.17, -55.7) * mm, "end": v(-12.55, -55.32) * mm});
            skArc(sketch, "E58.5.2", {"start": v(-12.4, -54.75) * mm, "mid": v(-12.48, -55.03) * mm, "end": v(-12.55, -55.32) * mm});
            skArc(sketch, "E58.5.3", {"start": v(-11.35, -54.53) * mm, "mid": v(-11.88, -54.6) * mm, "end": v(-12.4, -54.75) * mm});
            skLineSegment(sketch, "E58.5.4", {"start": v(-11.35, -54.53) * mm, "end": v(-10.26, -54.63) * mm});
            skLineSegment(sketch, "E58.6.0", {"start": v(-11.96, -59.15) * mm, "end": v(-10.88, -59.34) * mm});
            skArc(sketch, "E58.6.1", {"start": v(-11.96, -59.15) * mm, "mid": v(-12.45, -58.94) * mm, "end": v(-12.92, -58.67) * mm});
            skArc(sketch, "E58.6.2", {"start": v(-12.92, -58.08) * mm, "mid": v(-12.92, -58.38) * mm, "end": v(-12.92, -58.67) * mm});
            skArc(sketch, "E58.6.3", {"start": v(-11.96, -57.6) * mm, "mid": v(-12.45, -57.8) * mm, "end": v(-12.92, -58.08) * mm});
            skLineSegment(sketch, "E58.6.4", {"start": v(-11.96, -57.6) * mm, "end": v(-10.88, -57.41) * mm});
            skLineSegment(sketch, "E58.7.0", {"start": v(-11.35, -62.22) * mm, "end": v(-10.26, -62.12) * mm});
            skArc(sketch, "E58.7.1", {"start": v(-11.35, -62.22) * mm, "mid": v(-11.88, -62.15) * mm, "end": v(-12.4, -62) * mm});
            skArc(sketch, "E58.7.2", {"start": v(-12.55, -61.44) * mm, "mid": v(-12.48, -61.72) * mm, "end": v(-12.4, -62) * mm});
            skArc(sketch, "E58.7.3", {"start": v(-11.75, -60.72) * mm, "mid": v(-12.17, -61.05) * mm, "end": v(-12.55, -61.44) * mm});
            skLineSegment(sketch, "E58.7.4", {"start": v(-11.75, -60.72) * mm, "end": v(-10.76, -60.26) * mm});
            skLineSegment(sketch, "E58.8.0", {"start": v(-9.97, -65.02) * mm, "end": v(-8.94, -64.65) * mm});
            skArc(sketch, "E58.8.1", {"start": v(-9.97, -65.02) * mm, "mid": v(-10.5, -65.1) * mm, "end": v(-11.04, -65.09) * mm});
            skArc(sketch, "E58.8.2", {"start": v(-11.33, -64.58) * mm, "mid": v(-11.19, -64.84) * mm, "end": v(-11.04, -65.09) * mm});
            skArc(sketch, "E58.8.3", {"start": v(-10.74, -63.68) * mm, "mid": v(-11.07, -64.11) * mm, "end": v(-11.33, -64.58) * mm});
            skLineSegment(sketch, "E58.8.4", {"start": v(-10.74, -63.68) * mm, "end": v(-9.9, -62.98) * mm});
            skLineSegment(sketch, "E58.9.0", {"start": v(-7.9, -67.38) * mm, "end": v(-7, -66.75) * mm});
            skArc(sketch, "E58.9.1", {"start": v(-7.9, -67.38) * mm, "mid": v(-8.4, -67.58) * mm, "end": v(-8.93, -67.72) * mm});
            skArc(sketch, "E58.9.2", {"start": v(-9.34, -67.3) * mm, "mid": v(-9.14, -67.51) * mm, "end": v(-8.93, -67.72) * mm});
            skArc(sketch, "E58.9.3", {"start": v(-9, -66.28) * mm, "mid": v(-9.2, -66.78) * mm, "end": v(-9.34, -67.3) * mm});
            skLineSegment(sketch, "E58.9.4", {"start": v(-9, -66.28) * mm, "end": v(-8.37, -65.39) * mm});
            skLineSegment(sketch, "E58.10.0", {"start": v(-5.3, -69.12) * mm, "end": v(-4.6, -68.28) * mm});
            skArc(sketch, "E58.10.1", {"start": v(-5.3, -69.12) * mm, "mid": v(-5.74, -69.44) * mm, "end": v(-6.2, -69.7) * mm});
            skArc(sketch, "E58.10.2", {"start": v(-6.71, -69.42) * mm, "mid": v(-6.46, -69.57) * mm, "end": v(-6.2, -69.7) * mm});
            skArc(sketch, "E58.10.3", {"start": v(-6.65, -68.34) * mm, "mid": v(-6.72, -68.88) * mm, "end": v(-6.71, -69.42) * mm});
            skLineSegment(sketch, "E58.10.4", {"start": v(-6.65, -68.34) * mm, "end": v(-6.27, -67.31) * mm});
            skLineSegment(sketch, "E58.11.0", {"start": v(-2.35, -70.12) * mm, "end": v(-1.88, -69.13) * mm});
            skArc(sketch, "E58.11.1", {"start": v(-2.35, -70.12) * mm, "mid": v(-2.68, -70.55) * mm, "end": v(-3.06, -70.93) * mm});
            skArc(sketch, "E58.11.2", {"start": v(-3.63, -70.78) * mm, "mid": v(-3.34, -70.86) * mm, "end": v(-3.06, -70.93) * mm});
            skArc(sketch, "E58.11.3", {"start": v(-3.84, -69.72) * mm, "mid": v(-3.77, -70.26) * mm, "end": v(-3.63, -70.78) * mm});
            skLineSegment(sketch, "E58.11.4", {"start": v(-3.84, -69.72) * mm, "end": v(-3.75, -68.63) * mm});
            skLineSegment(sketch, "E58.12.0", {"start": v(0.77, -70.33) * mm, "end": v(0.96, -69.25) * mm});
            skArc(sketch, "E58.12.1", {"start": v(0.77, -70.33) * mm, "mid": v(0.57, -70.83) * mm, "end": v(0.3, -71.3) * mm});
            skArc(sketch, "E58.12.2", {"start": v(-0.3, -71.3) * mm, "mid": v(0, -71.3) * mm, "end": v(0.3, -71.3) * mm});
            skArc(sketch, "E58.12.3", {"start": v(-0.77, -70.33) * mm, "mid": v(-0.57, -70.83) * mm, "end": v(-0.3, -71.3) * mm});
            skLineSegment(sketch, "E58.12.4", {"start": v(-0.77, -70.33) * mm, "end": v(-0.96, -69.25) * mm});
            skLineSegment(sketch, "E58.13.0", {"start": v(3.84, -69.72) * mm, "end": v(3.75, -68.63) * mm});
            skArc(sketch, "E58.13.1", {"start": v(3.84, -69.72) * mm, "mid": v(3.77, -70.26) * mm, "end": v(3.63, -70.78) * mm});
            skArc(sketch, "E58.13.2", {"start": v(3.06, -70.93) * mm, "mid": v(3.34, -70.86) * mm, "end": v(3.63, -70.78) * mm});
            skArc(sketch, "E58.13.3", {"start": v(2.35, -70.12) * mm, "mid": v(2.68, -70.55) * mm, "end": v(3.06, -70.93) * mm});
            skLineSegment(sketch, "E58.13.4", {"start": v(2.35, -70.12) * mm, "end": v(1.88, -69.13) * mm});
            skLineSegment(sketch, "E58.14.0", {"start": v(6.65, -68.34) * mm, "end": v(6.27, -67.31) * mm});
            skArc(sketch, "E58.14.1", {"start": v(6.65, -68.34) * mm, "mid": v(6.72, -68.88) * mm, "end": v(6.71, -69.42) * mm});
            skArc(sketch, "E58.14.2", {"start": v(6.2, -69.7) * mm, "mid": v(6.46, -69.57) * mm, "end": v(6.71, -69.42) * mm});
            skArc(sketch, "E58.14.3", {"start": v(5.3, -69.12) * mm, "mid": v(5.74, -69.44) * mm, "end": v(6.2, -69.7) * mm});
            skLineSegment(sketch, "E58.14.4", {"start": v(5.3, -69.12) * mm, "end": v(4.6, -68.28) * mm});
            skLineSegment(sketch, "E58.15.0", {"start": v(9, -66.28) * mm, "end": v(8.37, -65.39) * mm});
            skArc(sketch, "E58.15.1", {"start": v(9, -66.28) * mm, "mid": v(9.2, -66.78) * mm, "end": v(9.34, -67.3) * mm});
            skArc(sketch, "E58.15.2", {"start": v(8.93, -67.72) * mm, "mid": v(9.14, -67.51) * mm, "end": v(9.34, -67.3) * mm});
            skArc(sketch, "E58.15.3", {"start": v(7.9, -67.38) * mm, "mid": v(8.4, -67.58) * mm, "end": v(8.93, -67.72) * mm});
            skLineSegment(sketch, "E58.15.4", {"start": v(7.9, -67.38) * mm, "end": v(7, -66.75) * mm});
            skLineSegment(sketch, "E58.16.0", {"start": v(10.74, -63.68) * mm, "end": v(9.9, -62.98) * mm});
            skArc(sketch, "E58.16.1", {"start": v(10.74, -63.68) * mm, "mid": v(11.07, -64.11) * mm, "end": v(11.33, -64.58) * mm});
            skArc(sketch, "E58.16.2", {"start": v(11.04, -65.09) * mm, "mid": v(11.19, -64.84) * mm, "end": v(11.33, -64.58) * mm});
            skArc(sketch, "E58.16.3", {"start": v(9.97, -65.02) * mm, "mid": v(10.5, -65.1) * mm, "end": v(11.04, -65.09) * mm});
            skLineSegment(sketch, "E58.16.4", {"start": v(9.97, -65.02) * mm, "end": v(8.94, -64.65) * mm});
            skLineSegment(sketch, "E58.17.0", {"start": v(11.75, -60.72) * mm, "end": v(10.76, -60.26) * mm});
            skArc(sketch, "E58.17.1", {"start": v(11.75, -60.72) * mm, "mid": v(12.17, -61.05) * mm, "end": v(12.55, -61.44) * mm});
            skArc(sketch, "E58.17.2", {"start": v(12.4, -62) * mm, "mid": v(12.48, -61.72) * mm, "end": v(12.55, -61.44) * mm});
            skArc(sketch, "E58.17.3", {"start": v(11.35, -62.22) * mm, "mid": v(11.88, -62.15) * mm, "end": v(12.4, -62) * mm});
            skLineSegment(sketch, "E58.17.4", {"start": v(11.35, -62.22) * mm, "end": v(10.26, -62.12) * mm});
            skLineSegment(sketch, "E58.18.0", {"start": v(11.96, -57.6) * mm, "end": v(10.88, -57.41) * mm});
            skArc(sketch, "E58.18.1", {"start": v(11.96, -57.6) * mm, "mid": v(12.45, -57.8) * mm, "end": v(12.92, -58.08) * mm});
            skArc(sketch, "E58.18.2", {"start": v(12.92, -58.67) * mm, "mid": v(12.92, -58.38) * mm, "end": v(12.92, -58.08) * mm});
            skArc(sketch, "E58.18.3", {"start": v(11.96, -59.15) * mm, "mid": v(12.45, -58.94) * mm, "end": v(12.92, -58.67) * mm});
            skLineSegment(sketch, "E58.18.4", {"start": v(11.96, -59.15) * mm, "end": v(10.88, -59.34) * mm});
            skLineSegment(sketch, "E58.19.0", {"start": v(11.35, -54.53) * mm, "end": v(10.26, -54.63) * mm});
            skArc(sketch, "E58.19.1", {"start": v(11.35, -54.53) * mm, "mid": v(11.88, -54.6) * mm, "end": v(12.4, -54.75) * mm});
            skArc(sketch, "E58.19.2", {"start": v(12.55, -55.32) * mm, "mid": v(12.48, -55.03) * mm, "end": v(12.4, -54.75) * mm});
            skArc(sketch, "E58.19.3", {"start": v(11.75, -56.03) * mm, "mid": v(12.17, -55.7) * mm, "end": v(12.55, -55.32) * mm});
            skLineSegment(sketch, "E58.19.4", {"start": v(11.75, -56.03) * mm, "end": v(10.76, -56.5) * mm});
            skLineSegment(sketch, "E58.20.0", {"start": v(9.97, -51.73) * mm, "end": v(8.94, -52.1) * mm});
            skArc(sketch, "E58.20.1", {"start": v(9.97, -51.73) * mm, "mid": v(10.5, -51.66) * mm, "end": v(11.04, -51.66) * mm});
            skArc(sketch, "E58.20.2", {"start": v(11.33, -52.17) * mm, "mid": v(11.19, -51.92) * mm, "end": v(11.04, -51.66) * mm});
            skArc(sketch, "E58.20.3", {"start": v(10.74, -53.07) * mm, "mid": v(11.07, -52.64) * mm, "end": v(11.33, -52.17) * mm});
            skLineSegment(sketch, "E58.20.4", {"start": v(10.74, -53.07) * mm, "end": v(9.9, -53.77) * mm});
            skLineSegment(sketch, "E58.21.0", {"start": v(7.9, -49.37) * mm, "end": v(7, -50) * mm});
            skArc(sketch, "E58.21.1", {"start": v(7.9, -49.37) * mm, "mid": v(8.4, -49.17) * mm, "end": v(8.93, -49.03) * mm});
            skArc(sketch, "E58.21.2", {"start": v(9.34, -49.45) * mm, "mid": v(9.14, -49.24) * mm, "end": v(8.93, -49.03) * mm});
            skArc(sketch, "E58.21.3", {"start": v(9, -50.47) * mm, "mid": v(9.2, -49.97) * mm, "end": v(9.34, -49.45) * mm});
            skLineSegment(sketch, "E58.21.4", {"start": v(9, -50.47) * mm, "end": v(8.37, -51.37) * mm});
            skLineSegment(sketch, "E58.22.0", {"start": v(5.3, -47.63) * mm, "end": v(4.6, -48.47) * mm});
            skArc(sketch, "E58.22.1", {"start": v(5.3, -47.63) * mm, "mid": v(5.74, -47.3) * mm, "end": v(6.2, -47.04) * mm});
            skArc(sketch, "E58.22.2", {"start": v(6.71, -47.34) * mm, "mid": v(6.46, -47.19) * mm, "end": v(6.2, -47.04) * mm});
            skArc(sketch, "E58.22.3", {"start": v(6.65, -48.4) * mm, "mid": v(6.72, -47.87) * mm, "end": v(6.71, -47.34) * mm});
            skLineSegment(sketch, "E58.22.4", {"start": v(6.65, -48.4) * mm, "end": v(6.27, -49.44) * mm});
            skLineSegment(sketch, "E58.23.0", {"start": v(2.35, -46.63) * mm, "end": v(1.88, -47.62) * mm});
            skArc(sketch, "E58.23.1", {"start": v(2.35, -46.63) * mm, "mid": v(2.68, -46.2) * mm, "end": v(3.06, -45.82) * mm});
            skArc(sketch, "E58.23.2", {"start": v(3.63, -45.97) * mm, "mid": v(3.34, -45.9) * mm, "end": v(3.06, -45.82) * mm});
            skArc(sketch, "E58.23.3", {"start": v(3.84, -47.03) * mm, "mid": v(3.77, -46.5) * mm, "end": v(3.63, -45.97) * mm});
            skLineSegment(sketch, "E58.23.4", {"start": v(3.84, -47.03) * mm, "end": v(3.75, -48.12) * mm});
            skArc(sketch, "E59", {"start": v(0.96, -47.5) * mm, "mid": v(1.43, -47.55) * mm, "end": v(1.88, -47.62) * mm});
            skArc(sketch, "E60.1.0", {"start": v(-1.88, -47.62) * mm, "mid": v(-1.43, -47.55) * mm, "end": v(-0.96, -47.5) * mm});
            skArc(sketch, "E60.2.0", {"start": v(-4.6, -48.47) * mm, "mid": v(-4.18, -48.29) * mm, "end": v(-3.75, -48.12) * mm});
            skArc(sketch, "E60.3.0", {"start": v(-7, -50) * mm, "mid": v(-6.65, -49.71) * mm, "end": v(-6.27, -49.44) * mm});
            skArc(sketch, "E60.4.0", {"start": v(-8.94, -52.1) * mm, "mid": v(-8.66, -51.73) * mm, "end": v(-8.37, -51.37) * mm});
            skArc(sketch, "E60.5.0", {"start": v(-10.26, -54.63) * mm, "mid": v(-10.09, -54.2) * mm, "end": v(-9.9, -53.77) * mm});
            skArc(sketch, "E60.6.0", {"start": v(-10.88, -57.41) * mm, "mid": v(-10.83, -56.95) * mm, "end": v(-10.76, -56.5) * mm});
            skArc(sketch, "E60.7.0", {"start": v(-10.76, -60.26) * mm, "mid": v(-10.83, -59.8) * mm, "end": v(-10.88, -59.34) * mm});
            skArc(sketch, "E60.8.0", {"start": v(-9.9, -62.98) * mm, "mid": v(-10.09, -62.55) * mm, "end": v(-10.26, -62.12) * mm});
            skArc(sketch, "E60.9.0", {"start": v(-8.37, -65.39) * mm, "mid": v(-8.66, -65.02) * mm, "end": v(-8.94, -64.65) * mm});
            skArc(sketch, "E60.10.0", {"start": v(-6.27, -67.31) * mm, "mid": v(-6.65, -67.04) * mm, "end": v(-7, -66.75) * mm});
            skArc(sketch, "E60.11.0", {"start": v(-3.75, -68.63) * mm, "mid": v(-4.18, -68.46) * mm, "end": v(-4.6, -68.28) * mm});
            skArc(sketch, "E60.12.0", {"start": v(-0.96, -69.25) * mm, "mid": v(-1.43, -69.2) * mm, "end": v(-1.88, -69.13) * mm});
            skArc(sketch, "E60.13.0", {"start": v(1.88, -69.13) * mm, "mid": v(1.43, -69.2) * mm, "end": v(0.96, -69.25) * mm});
            skArc(sketch, "E60.14.0", {"start": v(4.6, -68.28) * mm, "mid": v(4.18, -68.46) * mm, "end": v(3.75, -68.63) * mm});
            skArc(sketch, "E60.15.0", {"start": v(7, -66.75) * mm, "mid": v(6.65, -67.04) * mm, "end": v(6.27, -67.31) * mm});
            skArc(sketch, "E60.16.0", {"start": v(8.94, -64.65) * mm, "mid": v(8.66, -65.02) * mm, "end": v(8.37, -65.39) * mm});
            skArc(sketch, "E60.17.0", {"start": v(10.26, -62.12) * mm, "mid": v(10.09, -62.55) * mm, "end": v(9.9, -62.98) * mm});
            skArc(sketch, "E60.18.0", {"start": v(10.88, -59.34) * mm, "mid": v(10.83, -59.8) * mm, "end": v(10.76, -60.26) * mm});
            skArc(sketch, "E60.19.0", {"start": v(10.76, -56.5) * mm, "mid": v(10.83, -56.95) * mm, "end": v(10.88, -57.41) * mm});
            skArc(sketch, "E60.20.0", {"start": v(9.9, -53.77) * mm, "mid": v(10.09, -54.2) * mm, "end": v(10.26, -54.63) * mm});
            skArc(sketch, "E60.21.0", {"start": v(8.37, -51.37) * mm, "mid": v(8.66, -51.73) * mm, "end": v(8.94, -52.1) * mm});
            skArc(sketch, "E60.22.0", {"start": v(6.27, -49.44) * mm, "mid": v(6.65, -49.71) * mm, "end": v(7, -50) * mm});
            skArc(sketch, "E60.23.0", {"start": v(3.75, -48.12) * mm, "mid": v(4.18, -48.29) * mm, "end": v(4.6, -48.47) * mm});
            skCircle(sketch, "E61", {"center": v(0, -58.38) * mm, "radius": 6 * mm});
            skArc(sketch, "E62.1.0", {"start": v(-47.35, -62.87) * mm, "mid": v(-47.65, -62.51) * mm, "end": v(-48.03, -62.23) * mm});
            skArc(sketch, "E62.1.1", {"start": v(-48.77, -63.33) * mm, "mid": v(-48.74, -62.86) * mm, "end": v(-48.6, -62.42) * mm});
            skArc(sketch, "E62.2.0", {"start": v(-50.3, -64.1) * mm, "mid": v(-50.7, -63.86) * mm, "end": v(-51.14, -63.71) * mm});
            skArc(sketch, "E62.2.1", {"start": v(-51.5, -64.98) * mm, "mid": v(-51.61, -64.53) * mm, "end": v(-51.61, -64.06) * mm});
            skArc(sketch, "E62.3.0", {"start": v(-52.71, -66.2) * mm, "mid": v(-53.17, -66.08) * mm, "end": v(-53.64, -66.08) * mm});
            skArc(sketch, "E62.3.1", {"start": v(-53.6, -67.4) * mm, "mid": v(-53.84, -67) * mm, "end": v(-53.98, -66.56) * mm});
            skArc(sketch, "E62.4.0", {"start": v(-54.37, -68.93) * mm, "mid": v(-54.84, -68.96) * mm, "end": v(-55.28, -69.1) * mm});
            skArc(sketch, "E62.4.1", {"start": v(-54.83, -70.35) * mm, "mid": v(-55.19, -70.04) * mm, "end": v(-55.46, -69.66) * mm});
            skArc(sketch, "E62.5.0", {"start": v(-55.1, -72.04) * mm, "mid": v(-55.53, -72.21) * mm, "end": v(-55.91, -72.5) * mm});
            skArc(sketch, "E62.5.1", {"start": v(-55.1, -73.53) * mm, "mid": v(-55.53, -73.35) * mm, "end": v(-55.91, -73.08) * mm});
            skArc(sketch, "E62.6.0", {"start": v(-54.83, -75.22) * mm, "mid": v(-55.19, -75.52) * mm, "end": v(-55.46, -75.9) * mm});
            skArc(sketch, "E62.6.1", {"start": v(-54.37, -76.64) * mm, "mid": v(-54.84, -76.6) * mm, "end": v(-55.28, -76.46) * mm});
            skArc(sketch, "E62.7.0", {"start": v(-53.6, -78.16) * mm, "mid": v(-53.84, -78.56) * mm, "end": v(-53.98, -79) * mm});
            skArc(sketch, "E62.7.1", {"start": v(-52.71, -79.37) * mm, "mid": v(-53.17, -79.48) * mm, "end": v(-53.64, -79.48) * mm});
            skArc(sketch, "E62.8.0", {"start": v(-51.5, -80.58) * mm, "mid": v(-51.61, -81.04) * mm, "end": v(-51.61, -81.5) * mm});
            skArc(sketch, "E62.8.1", {"start": v(-50.3, -81.46) * mm, "mid": v(-50.7, -81.7) * mm, "end": v(-51.14, -81.85) * mm});
            skArc(sketch, "E62.9.0", {"start": v(-48.77, -82.24) * mm, "mid": v(-48.74, -82.7) * mm, "end": v(-48.6, -83.15) * mm});
            skArc(sketch, "E62.9.1", {"start": v(-47.35, -82.7) * mm, "mid": v(-47.65, -83.06) * mm, "end": v(-48.03, -83.33) * mm});
            skArc(sketch, "E62.10.0", {"start": v(-45.66, -82.97) * mm, "mid": v(-45.48, -83.4) * mm, "end": v(-45.2, -83.78) * mm});
            skArc(sketch, "E62.10.1", {"start": v(-44.17, -82.97) * mm, "mid": v(-44.35, -83.4) * mm, "end": v(-44.62, -83.78) * mm});
            skArc(sketch, "E62.11.0", {"start": v(-42.48, -82.7) * mm, "mid": v(-42.17, -83.06) * mm, "end": v(-41.8, -83.33) * mm});
            skArc(sketch, "E62.11.1", {"start": v(-41.06, -82.24) * mm, "mid": v(-41.1, -82.7) * mm, "end": v(-41.24, -83.15) * mm});
            skArc(sketch, "E62.12.0", {"start": v(-39.53, -81.46) * mm, "mid": v(-39.13, -81.7) * mm, "end": v(-38.69, -81.85) * mm});
            skArc(sketch, "E62.12.1", {"start": v(-38.32, -80.58) * mm, "mid": v(-38.21, -81.04) * mm, "end": v(-38.21, -81.5) * mm});
            skArc(sketch, "E62.13.0", {"start": v(-37.12, -79.37) * mm, "mid": v(-36.66, -79.48) * mm, "end": v(-36.2, -79.48) * mm});
            skArc(sketch, "E62.13.1", {"start": v(-36.24, -78.16) * mm, "mid": v(-36, -78.56) * mm, "end": v(-35.85, -79) * mm});
            skArc(sketch, "E62.14.0", {"start": v(-35.46, -76.64) * mm, "mid": v(-35, -76.6) * mm, "end": v(-34.55, -76.46) * mm});
            skArc(sketch, "E62.14.1", {"start": v(-35, -75.22) * mm, "mid": v(-34.64, -75.52) * mm, "end": v(-34.37, -75.9) * mm});
            skArc(sketch, "E62.15.0", {"start": v(-34.73, -73.53) * mm, "mid": v(-34.3, -73.35) * mm, "end": v(-33.92, -73.08) * mm});
            skArc(sketch, "E62.15.1", {"start": v(-34.73, -72.04) * mm, "mid": v(-34.3, -72.21) * mm, "end": v(-33.92, -72.5) * mm});
            skArc(sketch, "E62.16.0", {"start": v(-35, -70.35) * mm, "mid": v(-34.64, -70.04) * mm, "end": v(-34.37, -69.66) * mm});
            skArc(sketch, "E62.16.1", {"start": v(-35.46, -68.93) * mm, "mid": v(-35, -68.96) * mm, "end": v(-34.55, -69.1) * mm});
            skArc(sketch, "E62.17.0", {"start": v(-36.24, -67.4) * mm, "mid": v(-36, -67) * mm, "end": v(-35.85, -66.56) * mm});
            skArc(sketch, "E62.17.1", {"start": v(-37.12, -66.2) * mm, "mid": v(-36.66, -66.08) * mm, "end": v(-36.2, -66.08) * mm});
            skArc(sketch, "E62.18.0", {"start": v(-38.32, -64.98) * mm, "mid": v(-38.21, -64.53) * mm, "end": v(-38.21, -64.06) * mm});
            skArc(sketch, "E62.18.1", {"start": v(-39.53, -64.1) * mm, "mid": v(-39.13, -63.86) * mm, "end": v(-38.69, -63.71) * mm});
            skArc(sketch, "E62.19.0", {"start": v(-41.06, -63.33) * mm, "mid": v(-41.1, -62.86) * mm, "end": v(-41.24, -62.42) * mm});
            skArc(sketch, "E62.19.1", {"start": v(-42.48, -62.87) * mm, "mid": v(-42.17, -62.51) * mm, "end": v(-41.8, -62.23) * mm});
            skCircle(sketch, "E63", {"center": v(84.97, -81.06) * mm, "radius": 34.34 * mm, "construction": true});
            skCircle(sketch, "E64", {"center": v(84.97, -81.06) * mm, "radius": 45 * mm});
            skLineSegment(sketch, "E65", {"start": v(84.03, -81.06) * mm, "end": v(84.03, -46.3) * mm, "construction": true});
            skLineSegment(sketch, "E66", {"start": v(85.92, -81.06) * mm, "end": v(85.92, -46.29) * mm, "construction": true});
            skLineSegment(sketch, "E67", {"start": v(84.97, -81.06) * mm, "end": v(84.97, -46.2) * mm, "construction": true});
            skPoint(sketch, "E68", {"position": v(85.92, -46.73) * mm});
            skPoint(sketch, "E69", {"position": v(84.03, -46.73) * mm});
            skLineSegment(sketch, "E70", {"start": v(85.92, -46.73) * mm, "end": v(86.1, -47.78) * mm});
            skLineSegment(sketch, "E71", {"start": v(85.92, -46.73) * mm, "end": v(85.75, -45.77) * mm});
            skLineSegment(sketch, "E72.MirrorCS", {"start": v(84.03, -46.73) * mm, "end": v(83.85, -47.78) * mm});
            skLineSegment(sketch, "E73.MirrorCS", {"start": v(84.03, -46.73) * mm, "end": v(84.2, -45.77) * mm});
            skLineSegment(sketch, "E74.1.0", {"start": v(80.87, -46.97) * mm, "end": v(80.78, -48.02) * mm});
            skLineSegment(sketch, "E74.1.1", {"start": v(80.87, -46.97) * mm, "end": v(80.95, -46) * mm});
            skLineSegment(sketch, "E74.1.2", {"start": v(82.74, -46.8) * mm, "end": v(82.49, -45.85) * mm});
            skLineSegment(sketch, "E74.1.3", {"start": v(82.74, -46.8) * mm, "end": v(83.02, -47.82) * mm});
            skLineSegment(sketch, "E74.2.0", {"start": v(77.74, -47.5) * mm, "end": v(77.75, -48.55) * mm});
            skLineSegment(sketch, "E74.2.1", {"start": v(77.74, -47.5) * mm, "end": v(77.73, -46.51) * mm});
            skLineSegment(sketch, "E74.2.2", {"start": v(79.6, -47.14) * mm, "end": v(79.25, -46.23) * mm});
            skLineSegment(sketch, "E74.2.3", {"start": v(79.6, -47.14) * mm, "end": v(79.97, -48.14) * mm});
            skLineSegment(sketch, "E74.3.0", {"start": v(74.67, -48.3) * mm, "end": v(74.78, -49.36) * mm});
            skLineSegment(sketch, "E74.3.1", {"start": v(74.67, -48.3) * mm, "end": v(74.57, -47.33) * mm});
            skLineSegment(sketch, "E74.3.2", {"start": v(76.49, -47.78) * mm, "end": v(76.06, -46.9) * mm});
            skLineSegment(sketch, "E74.3.3", {"start": v(76.49, -47.78) * mm, "end": v(76.95, -48.74) * mm});
            skLineSegment(sketch, "E74.4.0", {"start": v(71.7, -49.4) * mm, "end": v(71.9, -50.43) * mm});
            skLineSegment(sketch, "E74.4.1", {"start": v(71.7, -49.4) * mm, "end": v(71.5, -48.43) * mm});
            skLineSegment(sketch, "E74.4.2", {"start": v(73.45, -48.7) * mm, "end": v(72.94, -47.87) * mm});
            skLineSegment(sketch, "E74.4.3", {"start": v(73.45, -48.7) * mm, "end": v(74, -49.62) * mm});
            skLineSegment(sketch, "E74.5.0", {"start": v(68.83, -50.75) * mm, "end": v(69.13, -51.77) * mm});
            skLineSegment(sketch, "E74.5.1", {"start": v(68.83, -50.75) * mm, "end": v(68.55, -49.81) * mm});
            skLineSegment(sketch, "E74.5.2", {"start": v(70.52, -49.91) * mm, "end": v(69.93, -49.12) * mm});
            skLineSegment(sketch, "E74.5.3", {"start": v(70.52, -49.91) * mm, "end": v(71.15, -50.77) * mm});
            skLineSegment(sketch, "E74.6.0", {"start": v(66.1, -52.37) * mm, "end": v(66.5, -53.36) * mm});
            skLineSegment(sketch, "E74.6.1", {"start": v(66.1, -52.37) * mm, "end": v(65.74, -51.46) * mm});
            skLineSegment(sketch, "E74.6.2", {"start": v(67.7, -51.38) * mm, "end": v(67.05, -50.65) * mm});
            skLineSegment(sketch, "E74.6.3", {"start": v(67.7, -51.38) * mm, "end": v(68.41, -52.17) * mm});
            skLineSegment(sketch, "E74.7.0", {"start": v(63.53, -54.23) * mm, "end": v(64.02, -55.18) * mm});
            skLineSegment(sketch, "E74.7.1", {"start": v(63.53, -54.23) * mm, "end": v(63.09, -53.36) * mm});
            skLineSegment(sketch, "E74.7.2", {"start": v(65.04, -53.1) * mm, "end": v(64.32, -52.43) * mm});
            skLineSegment(sketch, "E74.7.3", {"start": v(65.04, -53.1) * mm, "end": v(65.82, -53.82) * mm});
            skLineSegment(sketch, "E74.8.0", {"start": v(61.15, -56.33) * mm, "end": v(61.72, -57.22) * mm});
            skLineSegment(sketch, "E74.8.1", {"start": v(61.15, -56.33) * mm, "end": v(60.63, -55.5) * mm});
            skLineSegment(sketch, "E74.8.2", {"start": v(62.54, -55.06) * mm, "end": v(61.77, -54.46) * mm});
            skLineSegment(sketch, "E74.8.3", {"start": v(62.54, -55.06) * mm, "end": v(63.38, -55.7) * mm});
            skLineSegment(sketch, "E74.9.0", {"start": v(58.97, -58.63) * mm, "end": v(59.62, -59.47) * mm});
            skLineSegment(sketch, "E74.9.1", {"start": v(58.97, -58.63) * mm, "end": v(58.37, -57.86) * mm});
            skLineSegment(sketch, "E74.9.2", {"start": v(60.24, -57.24) * mm, "end": v(59.41, -56.71) * mm});
            skLineSegment(sketch, "E74.9.3", {"start": v(60.24, -57.24) * mm, "end": v(61.14, -57.8) * mm});
            skLineSegment(sketch, "E74.10.0", {"start": v(57.01, -61.13) * mm, "end": v(57.74, -61.9) * mm});
            skLineSegment(sketch, "E74.10.1", {"start": v(57.01, -61.13) * mm, "end": v(56.34, -60.4) * mm});
            skLineSegment(sketch, "E74.10.2", {"start": v(58.15, -59.62) * mm, "end": v(57.28, -59.18) * mm});
            skLineSegment(sketch, "E74.10.3", {"start": v(58.15, -59.62) * mm, "end": v(59.1, -60.1) * mm});
            skLineSegment(sketch, "E74.11.0", {"start": v(55.3, -63.8) * mm, "end": v(56.08, -64.5) * mm});
            skLineSegment(sketch, "E74.11.1", {"start": v(55.3, -63.8) * mm, "end": v(54.56, -63.14) * mm});
            skLineSegment(sketch, "E74.11.2", {"start": v(56.28, -62.19) * mm, "end": v(55.37, -61.82) * mm});
            skLineSegment(sketch, "E74.11.3", {"start": v(56.28, -62.19) * mm, "end": v(57.27, -62.58) * mm});
            skLineSegment(sketch, "E74.12.0", {"start": v(53.82, -66.6) * mm, "end": v(54.68, -67.23) * mm});
            skLineSegment(sketch, "E74.12.1", {"start": v(53.82, -66.6) * mm, "end": v(53.04, -66.02) * mm});
            skLineSegment(sketch, "E74.12.2", {"start": v(54.66, -64.92) * mm, "end": v(53.73, -64.64) * mm});
            skLineSegment(sketch, "E74.12.3", {"start": v(54.66, -64.92) * mm, "end": v(55.68, -65.22) * mm});
            skLineSegment(sketch, "E74.13.0", {"start": v(52.62, -69.54) * mm, "end": v(53.53, -70.09) * mm});
            skLineSegment(sketch, "E74.13.1", {"start": v(52.62, -69.54) * mm, "end": v(51.79, -69.03) * mm});
            skLineSegment(sketch, "E74.13.2", {"start": v(53.3, -67.78) * mm, "end": v(52.34, -67.6) * mm});
            skLineSegment(sketch, "E74.13.3", {"start": v(53.3, -67.78) * mm, "end": v(54.35, -67.99) * mm});
            skLineSegment(sketch, "E74.14.0", {"start": v(51.7, -72.57) * mm, "end": v(52.65, -73.04) * mm});
            skLineSegment(sketch, "E74.14.1", {"start": v(51.7, -72.57) * mm, "end": v(50.82, -72.14) * mm});
            skLineSegment(sketch, "E74.14.2", {"start": v(52.21, -70.76) * mm, "end": v(51.24, -70.66) * mm});
            skLineSegment(sketch, "E74.14.3", {"start": v(52.21, -70.76) * mm, "end": v(53.27, -70.87) * mm});
            skLineSegment(sketch, "E74.15.0", {"start": v(51.06, -75.68) * mm, "end": v(52.05, -76.05) * mm});
            skLineSegment(sketch, "E74.15.1", {"start": v(51.06, -75.68) * mm, "end": v(50.14, -75.33) * mm});
            skLineSegment(sketch, "E74.15.2", {"start": v(51.4, -73.83) * mm, "end": v(50.42, -73.82) * mm});
            skLineSegment(sketch, "E74.15.3", {"start": v(51.4, -73.83) * mm, "end": v(52.47, -73.84) * mm});
            skLineSegment(sketch, "E74.16.0", {"start": v(50.7, -78.83) * mm, "end": v(51.73, -79.11) * mm});
            skLineSegment(sketch, "E74.16.1", {"start": v(50.7, -78.83) * mm, "end": v(49.76, -78.57) * mm});
            skLineSegment(sketch, "E74.16.2", {"start": v(50.88, -76.95) * mm, "end": v(49.9, -77.03) * mm});
            skLineSegment(sketch, "E74.16.3", {"start": v(50.88, -76.95) * mm, "end": v(51.94, -76.87) * mm});
            skLineSegment(sketch, "E74.17.0", {"start": v(50.65, -82) * mm, "end": v(51.7, -82.19) * mm});
            skLineSegment(sketch, "E74.17.1", {"start": v(50.65, -82) * mm, "end": v(49.68, -81.83) * mm});
            skLineSegment(sketch, "E74.17.2", {"start": v(50.65, -80.12) * mm, "end": v(49.68, -80.29) * mm});
            skLineSegment(sketch, "E74.17.3", {"start": v(50.65, -80.12) * mm, "end": v(51.7, -79.93) * mm});
            skLineSegment(sketch, "E74.18.0", {"start": v(50.88, -85.17) * mm, "end": v(51.94, -85.25) * mm});
            skLineSegment(sketch, "E74.18.1", {"start": v(50.88, -85.17) * mm, "end": v(49.9, -85.09) * mm});
            skLineSegment(sketch, "E74.18.2", {"start": v(50.7, -83.29) * mm, "end": v(49.76, -83.55) * mm});
            skLineSegment(sketch, "E74.18.3", {"start": v(50.7, -83.29) * mm, "end": v(51.73, -83) * mm});
            skLineSegment(sketch, "E74.19.0", {"start": v(51.4, -88.3) * mm, "end": v(52.47, -88.28) * mm});
            skLineSegment(sketch, "E74.19.1", {"start": v(51.4, -88.3) * mm, "end": v(50.42, -88.3) * mm});
            skLineSegment(sketch, "E74.19.2", {"start": v(51.06, -86.44) * mm, "end": v(50.14, -86.79) * mm});
            skLineSegment(sketch, "E74.19.3", {"start": v(51.06, -86.44) * mm, "end": v(52.05, -86.07) * mm});
            skLineSegment(sketch, "E74.20.0", {"start": v(52.21, -91.36) * mm, "end": v(53.27, -91.25) * mm});
            skLineSegment(sketch, "E74.20.1", {"start": v(52.21, -91.36) * mm, "end": v(51.24, -91.46) * mm});
            skLineSegment(sketch, "E74.20.2", {"start": v(51.7, -89.55) * mm, "end": v(50.82, -89.97) * mm});
            skLineSegment(sketch, "E74.20.3", {"start": v(51.7, -89.55) * mm, "end": v(52.65, -89.08) * mm});
            skLineSegment(sketch, "E74.21.0", {"start": v(53.3, -94.34) * mm, "end": v(54.35, -94.13) * mm});
            skLineSegment(sketch, "E74.21.1", {"start": v(53.3, -94.34) * mm, "end": v(52.34, -94.53) * mm});
            skLineSegment(sketch, "E74.21.2", {"start": v(52.62, -92.58) * mm, "end": v(51.79, -93.09) * mm});
            skLineSegment(sketch, "E74.21.3", {"start": v(52.62, -92.58) * mm, "end": v(53.53, -92.03) * mm});
            skLineSegment(sketch, "E74.22.0", {"start": v(54.66, -97.2) * mm, "end": v(55.68, -96.9) * mm});
            skLineSegment(sketch, "E74.22.1", {"start": v(54.66, -97.2) * mm, "end": v(53.73, -97.48) * mm});
            skLineSegment(sketch, "E74.22.2", {"start": v(53.82, -95.52) * mm, "end": v(53.04, -96.1) * mm});
            skLineSegment(sketch, "E74.22.3", {"start": v(53.82, -95.52) * mm, "end": v(54.68, -94.89) * mm});
            skLineSegment(sketch, "E74.23.0", {"start": v(56.28, -99.93) * mm, "end": v(57.27, -99.54) * mm});
            skLineSegment(sketch, "E74.23.1", {"start": v(56.28, -99.93) * mm, "end": v(55.37, -100.3) * mm});
            skLineSegment(sketch, "E74.23.2", {"start": v(55.3, -98.33) * mm, "end": v(54.56, -98.98) * mm});
            skLineSegment(sketch, "E74.23.3", {"start": v(55.3, -98.33) * mm, "end": v(56.08, -97.62) * mm});
            skLineSegment(sketch, "E74.24.0", {"start": v(58.15, -102.5) * mm, "end": v(59.1, -102.02) * mm});
            skLineSegment(sketch, "E74.24.1", {"start": v(58.15, -102.5) * mm, "end": v(57.28, -102.94) * mm});
            skLineSegment(sketch, "E74.24.2", {"start": v(57.01, -101) * mm, "end": v(56.34, -101.71) * mm});
            skLineSegment(sketch, "E74.24.3", {"start": v(57.01, -101) * mm, "end": v(57.74, -100.22) * mm});
            skLineSegment(sketch, "E74.25.0", {"start": v(60.24, -104.88) * mm, "end": v(61.14, -104.31) * mm});
            skLineSegment(sketch, "E74.25.1", {"start": v(60.24, -104.88) * mm, "end": v(59.41, -105.4) * mm});
            skLineSegment(sketch, "E74.25.2", {"start": v(58.97, -103.49) * mm, "end": v(58.37, -104.26) * mm});
            skLineSegment(sketch, "E74.25.3", {"start": v(58.97, -103.49) * mm, "end": v(59.62, -102.65) * mm});
            skLineSegment(sketch, "E74.26.0", {"start": v(62.54, -107.06) * mm, "end": v(63.38, -106.41) * mm});
            skLineSegment(sketch, "E74.26.1", {"start": v(62.54, -107.06) * mm, "end": v(61.77, -107.66) * mm});
            skLineSegment(sketch, "E74.26.2", {"start": v(61.15, -105.8) * mm, "end": v(60.63, -106.62) * mm});
            skLineSegment(sketch, "E74.26.3", {"start": v(61.15, -105.8) * mm, "end": v(61.72, -104.9) * mm});
            skLineSegment(sketch, "E74.27.0", {"start": v(65.04, -109.02) * mm, "end": v(65.82, -108.3) * mm});
            skLineSegment(sketch, "E74.27.1", {"start": v(65.04, -109.02) * mm, "end": v(64.32, -109.69) * mm});
            skLineSegment(sketch, "E74.27.2", {"start": v(63.53, -107.89) * mm, "end": v(63.09, -108.76) * mm});
            skLineSegment(sketch, "E74.27.3", {"start": v(63.53, -107.89) * mm, "end": v(64.02, -106.94) * mm});
            skLineSegment(sketch, "E74.28.0", {"start": v(67.7, -110.74) * mm, "end": v(68.41, -109.95) * mm});
            skLineSegment(sketch, "E74.28.1", {"start": v(67.7, -110.74) * mm, "end": v(67.05, -111.47) * mm});
            skLineSegment(sketch, "E74.28.2", {"start": v(66.1, -109.75) * mm, "end": v(65.74, -110.66) * mm});
            skLineSegment(sketch, "E74.28.3", {"start": v(66.1, -109.75) * mm, "end": v(66.5, -108.76) * mm});
            skLineSegment(sketch, "E74.29.0", {"start": v(70.52, -112.2) * mm, "end": v(71.15, -111.35) * mm});
            skLineSegment(sketch, "E74.29.1", {"start": v(70.52, -112.2) * mm, "end": v(69.93, -113) * mm});
            skLineSegment(sketch, "E74.29.2", {"start": v(68.83, -111.37) * mm, "end": v(68.55, -112.3) * mm});
            skLineSegment(sketch, "E74.29.3", {"start": v(68.83, -111.37) * mm, "end": v(69.13, -110.35) * mm});
            skLineSegment(sketch, "E74.30.0", {"start": v(73.45, -113.4) * mm, "end": v(74, -112.5) * mm});
            skLineSegment(sketch, "E74.30.1", {"start": v(73.45, -113.4) * mm, "end": v(72.94, -114.25) * mm});
            skLineSegment(sketch, "E74.30.2", {"start": v(71.7, -112.73) * mm, "end": v(71.5, -113.69) * mm});
            skLineSegment(sketch, "E74.30.3", {"start": v(71.7, -112.73) * mm, "end": v(71.9, -111.69) * mm});
            skLineSegment(sketch, "E74.31.0", {"start": v(76.49, -114.33) * mm, "end": v(76.95, -113.38) * mm});
            skLineSegment(sketch, "E74.31.1", {"start": v(76.49, -114.33) * mm, "end": v(76.06, -115.22) * mm});
            skLineSegment(sketch, "E74.31.2", {"start": v(74.67, -113.82) * mm, "end": v(74.57, -114.8) * mm});
            skLineSegment(sketch, "E74.31.3", {"start": v(74.67, -113.82) * mm, "end": v(74.78, -112.76) * mm});
            skLineSegment(sketch, "E74.32.0", {"start": v(79.6, -114.98) * mm, "end": v(79.97, -113.98) * mm});
            skLineSegment(sketch, "E74.32.1", {"start": v(79.6, -114.98) * mm, "end": v(79.25, -115.9) * mm});
            skLineSegment(sketch, "E74.32.2", {"start": v(77.74, -114.63) * mm, "end": v(77.73, -115.6) * mm});
            skLineSegment(sketch, "E74.32.3", {"start": v(77.74, -114.63) * mm, "end": v(77.75, -113.57) * mm});
            skLineSegment(sketch, "E74.33.0", {"start": v(82.74, -115.33) * mm, "end": v(83.02, -114.3) * mm});
            skLineSegment(sketch, "E74.33.1", {"start": v(82.74, -115.33) * mm, "end": v(82.49, -116.27) * mm});
            skLineSegment(sketch, "E74.33.2", {"start": v(80.87, -115.15) * mm, "end": v(80.95, -116.13) * mm});
            skLineSegment(sketch, "E74.33.3", {"start": v(80.87, -115.15) * mm, "end": v(80.78, -114.1) * mm});
            skLineSegment(sketch, "E74.34.0", {"start": v(85.92, -115.39) * mm, "end": v(86.1, -114.34) * mm});
            skLineSegment(sketch, "E74.34.1", {"start": v(85.92, -115.39) * mm, "end": v(85.75, -116.35) * mm});
            skLineSegment(sketch, "E74.34.2", {"start": v(84.03, -115.39) * mm, "end": v(84.2, -116.35) * mm});
            skLineSegment(sketch, "E74.34.3", {"start": v(84.03, -115.39) * mm, "end": v(83.85, -114.34) * mm});
            skLineSegment(sketch, "E74.35.0", {"start": v(89.08, -115.15) * mm, "end": v(89.17, -114.1) * mm});
            skLineSegment(sketch, "E74.35.1", {"start": v(89.08, -115.15) * mm, "end": v(89, -116.13) * mm});
            skLineSegment(sketch, "E74.35.2", {"start": v(87.2, -115.33) * mm, "end": v(87.46, -116.27) * mm});
            skLineSegment(sketch, "E74.35.3", {"start": v(87.2, -115.33) * mm, "end": v(86.92, -114.3) * mm});
            skLineSegment(sketch, "E74.36.0", {"start": v(92.2, -114.63) * mm, "end": v(92.2, -113.57) * mm});
            skLineSegment(sketch, "E74.36.1", {"start": v(92.2, -114.63) * mm, "end": v(92.22, -115.6) * mm});
            skLineSegment(sketch, "E74.36.2", {"start": v(90.35, -114.98) * mm, "end": v(90.7, -115.9) * mm});
            skLineSegment(sketch, "E74.36.3", {"start": v(90.35, -114.98) * mm, "end": v(89.98, -113.98) * mm});
            skLineSegment(sketch, "E74.37.0", {"start": v(95.27, -113.82) * mm, "end": v(95.17, -112.76) * mm});
            skLineSegment(sketch, "E74.37.1", {"start": v(95.27, -113.82) * mm, "end": v(95.37, -114.8) * mm});
            skLineSegment(sketch, "E74.37.2", {"start": v(93.46, -114.33) * mm, "end": v(93.89, -115.22) * mm});
            skLineSegment(sketch, "E74.37.3", {"start": v(93.46, -114.33) * mm, "end": v(93, -113.38) * mm});
            skLineSegment(sketch, "E74.38.0", {"start": v(98.25, -112.73) * mm, "end": v(98.05, -111.69) * mm});
            skLineSegment(sketch, "E74.38.1", {"start": v(98.25, -112.73) * mm, "end": v(98.44, -113.69) * mm});
            skLineSegment(sketch, "E74.38.2", {"start": v(96.5, -113.4) * mm, "end": v(97, -114.25) * mm});
            skLineSegment(sketch, "E74.38.3", {"start": v(96.5, -113.4) * mm, "end": v(95.94, -112.5) * mm});
            skLineSegment(sketch, "E74.39.0", {"start": v(101.12, -111.37) * mm, "end": v(100.82, -110.35) * mm});
            skLineSegment(sketch, "E74.39.1", {"start": v(101.12, -111.37) * mm, "end": v(101.4, -112.3) * mm});
            skLineSegment(sketch, "E74.39.2", {"start": v(99.43, -112.2) * mm, "end": v(100.01, -113) * mm});
            skLineSegment(sketch, "E74.39.3", {"start": v(99.43, -112.2) * mm, "end": v(98.8, -111.35) * mm});
            skLineSegment(sketch, "E74.40.0", {"start": v(103.85, -109.75) * mm, "end": v(103.45, -108.76) * mm});
            skLineSegment(sketch, "E74.40.1", {"start": v(103.85, -109.75) * mm, "end": v(104.2, -110.66) * mm});
            skLineSegment(sketch, "E74.40.2", {"start": v(102.24, -110.74) * mm, "end": v(102.9, -111.47) * mm});
            skLineSegment(sketch, "E74.40.3", {"start": v(102.24, -110.74) * mm, "end": v(101.54, -109.95) * mm});
            skLineSegment(sketch, "E74.41.0", {"start": v(106.41, -107.89) * mm, "end": v(105.93, -106.94) * mm});
            skLineSegment(sketch, "E74.41.1", {"start": v(106.41, -107.89) * mm, "end": v(106.86, -108.76) * mm});
            skLineSegment(sketch, "E74.41.2", {"start": v(104.9, -109.02) * mm, "end": v(105.62, -109.69) * mm});
            skLineSegment(sketch, "E74.41.3", {"start": v(104.9, -109.02) * mm, "end": v(104.13, -108.3) * mm});
            skLineSegment(sketch, "E74.42.0", {"start": v(108.8, -105.8) * mm, "end": v(108.23, -104.9) * mm});
            skLineSegment(sketch, "E74.42.1", {"start": v(108.8, -105.8) * mm, "end": v(109.32, -106.62) * mm});
            skLineSegment(sketch, "E74.42.2", {"start": v(107.4, -107.06) * mm, "end": v(108.18, -107.66) * mm});
            skLineSegment(sketch, "E74.42.3", {"start": v(107.4, -107.06) * mm, "end": v(106.56, -106.41) * mm});
            skLineSegment(sketch, "E74.43.0", {"start": v(110.98, -103.49) * mm, "end": v(110.33, -102.65) * mm});
            skLineSegment(sketch, "E74.43.1", {"start": v(110.98, -103.49) * mm, "end": v(111.57, -104.26) * mm});
            skLineSegment(sketch, "E74.43.2", {"start": v(109.7, -104.88) * mm, "end": v(110.53, -105.4) * mm});
            skLineSegment(sketch, "E74.43.3", {"start": v(109.7, -104.88) * mm, "end": v(108.8, -104.31) * mm});
            skLineSegment(sketch, "E74.44.0", {"start": v(112.94, -101) * mm, "end": v(112.21, -100.22) * mm});
            skLineSegment(sketch, "E74.44.1", {"start": v(112.94, -101) * mm, "end": v(113.6, -101.71) * mm});
            skLineSegment(sketch, "E74.44.2", {"start": v(111.8, -102.5) * mm, "end": v(112.67, -102.94) * mm});
            skLineSegment(sketch, "E74.44.3", {"start": v(111.8, -102.5) * mm, "end": v(110.85, -102.02) * mm});
            skLineSegment(sketch, "E74.45.0", {"start": v(114.66, -98.33) * mm, "end": v(113.86, -97.62) * mm});
            skLineSegment(sketch, "E74.45.1", {"start": v(114.66, -98.33) * mm, "end": v(115.39, -98.98) * mm});
            skLineSegment(sketch, "E74.45.2", {"start": v(113.66, -99.93) * mm, "end": v(114.57, -100.3) * mm});
            skLineSegment(sketch, "E74.45.3", {"start": v(113.66, -99.93) * mm, "end": v(112.68, -99.54) * mm});
            skLineSegment(sketch, "E74.46.0", {"start": v(116.12, -95.52) * mm, "end": v(115.27, -94.89) * mm});
            skLineSegment(sketch, "E74.46.1", {"start": v(116.12, -95.52) * mm, "end": v(116.9, -96.1) * mm});
            skLineSegment(sketch, "E74.46.2", {"start": v(115.28, -97.2) * mm, "end": v(116.22, -97.48) * mm});
            skLineSegment(sketch, "E74.46.3", {"start": v(115.28, -97.2) * mm, "end": v(114.26, -96.9) * mm});
            skLineSegment(sketch, "E74.47.0", {"start": v(117.32, -92.58) * mm, "end": v(116.41, -92.03) * mm});
            skLineSegment(sketch, "E74.47.1", {"start": v(117.32, -92.58) * mm, "end": v(118.16, -93.09) * mm});
            skLineSegment(sketch, "E74.47.2", {"start": v(116.64, -94.34) * mm, "end": v(117.6, -94.53) * mm});
            skLineSegment(sketch, "E74.47.3", {"start": v(116.64, -94.34) * mm, "end": v(115.6, -94.13) * mm});
            skLineSegment(sketch, "E74.48.0", {"start": v(118.25, -89.55) * mm, "end": v(117.3, -89.08) * mm});
            skLineSegment(sketch, "E74.48.1", {"start": v(118.25, -89.55) * mm, "end": v(119.13, -89.97) * mm});
            skLineSegment(sketch, "E74.48.2", {"start": v(117.73, -91.36) * mm, "end": v(118.7, -91.46) * mm});
            skLineSegment(sketch, "E74.48.3", {"start": v(117.73, -91.36) * mm, "end": v(116.68, -91.25) * mm});
            skLineSegment(sketch, "E74.49.0", {"start": v(118.89, -86.44) * mm, "end": v(117.9, -86.07) * mm});
            skLineSegment(sketch, "E74.49.1", {"start": v(118.89, -86.44) * mm, "end": v(119.8, -86.79) * mm});
            skLineSegment(sketch, "E74.49.2", {"start": v(118.54, -88.3) * mm, "end": v(119.52, -88.3) * mm});
            skLineSegment(sketch, "E74.49.3", {"start": v(118.54, -88.3) * mm, "end": v(117.48, -88.28) * mm});
            skLineSegment(sketch, "E74.50.0", {"start": v(119.24, -83.29) * mm, "end": v(118.22, -83) * mm});
            skLineSegment(sketch, "E74.50.1", {"start": v(119.24, -83.29) * mm, "end": v(120.19, -83.55) * mm});
            skLineSegment(sketch, "E74.50.2", {"start": v(119.07, -85.17) * mm, "end": v(120.04, -85.09) * mm});
            skLineSegment(sketch, "E74.50.3", {"start": v(119.07, -85.17) * mm, "end": v(118, -85.25) * mm});
            skLineSegment(sketch, "E74.51.0", {"start": v(119.3, -80.12) * mm, "end": v(118.25, -79.93) * mm});
            skLineSegment(sketch, "E74.51.1", {"start": v(119.3, -80.12) * mm, "end": v(120.26, -80.29) * mm});
            skLineSegment(sketch, "E74.51.2", {"start": v(119.3, -82) * mm, "end": v(120.26, -81.83) * mm});
            skLineSegment(sketch, "E74.51.3", {"start": v(119.3, -82) * mm, "end": v(118.25, -82.19) * mm});
            skLineSegment(sketch, "E74.52.0", {"start": v(119.07, -76.95) * mm, "end": v(118, -76.87) * mm});
            skLineSegment(sketch, "E74.52.1", {"start": v(119.07, -76.95) * mm, "end": v(120.04, -77.03) * mm});
            skLineSegment(sketch, "E74.52.2", {"start": v(119.24, -78.83) * mm, "end": v(120.19, -78.57) * mm});
            skLineSegment(sketch, "E74.52.3", {"start": v(119.24, -78.83) * mm, "end": v(118.22, -79.11) * mm});
            skLineSegment(sketch, "E74.53.0", {"start": v(118.54, -73.83) * mm, "end": v(117.48, -73.84) * mm});
            skLineSegment(sketch, "E74.53.1", {"start": v(118.54, -73.83) * mm, "end": v(119.52, -73.82) * mm});
            skLineSegment(sketch, "E74.53.2", {"start": v(118.89, -75.68) * mm, "end": v(119.8, -75.33) * mm});
            skLineSegment(sketch, "E74.53.3", {"start": v(118.89, -75.68) * mm, "end": v(117.9, -76.05) * mm});
            skLineSegment(sketch, "E74.54.0", {"start": v(117.73, -70.76) * mm, "end": v(116.68, -70.87) * mm});
            skLineSegment(sketch, "E74.54.1", {"start": v(117.73, -70.76) * mm, "end": v(118.7, -70.66) * mm});
            skLineSegment(sketch, "E74.54.2", {"start": v(118.25, -72.57) * mm, "end": v(119.13, -72.14) * mm});
            skLineSegment(sketch, "E74.54.3", {"start": v(118.25, -72.57) * mm, "end": v(117.3, -73.04) * mm});
            skLineSegment(sketch, "E74.55.0", {"start": v(116.64, -67.78) * mm, "end": v(115.6, -67.99) * mm});
            skLineSegment(sketch, "E74.55.1", {"start": v(116.64, -67.78) * mm, "end": v(117.6, -67.6) * mm});
            skLineSegment(sketch, "E74.55.2", {"start": v(117.32, -69.54) * mm, "end": v(118.16, -69.03) * mm});
            skLineSegment(sketch, "E74.55.3", {"start": v(117.32, -69.54) * mm, "end": v(116.41, -70.09) * mm});
            skLineSegment(sketch, "E74.56.0", {"start": v(115.28, -64.92) * mm, "end": v(114.26, -65.22) * mm});
            skLineSegment(sketch, "E74.56.1", {"start": v(115.28, -64.92) * mm, "end": v(116.22, -64.64) * mm});
            skLineSegment(sketch, "E74.56.2", {"start": v(116.12, -66.6) * mm, "end": v(116.9, -66.02) * mm});
            skLineSegment(sketch, "E74.56.3", {"start": v(116.12, -66.6) * mm, "end": v(115.27, -67.23) * mm});
            skLineSegment(sketch, "E74.57.0", {"start": v(113.66, -62.19) * mm, "end": v(112.68, -62.58) * mm});
            skLineSegment(sketch, "E74.57.1", {"start": v(113.66, -62.19) * mm, "end": v(114.57, -61.82) * mm});
            skLineSegment(sketch, "E74.57.2", {"start": v(114.66, -63.8) * mm, "end": v(115.39, -63.14) * mm});
            skLineSegment(sketch, "E74.57.3", {"start": v(114.66, -63.8) * mm, "end": v(113.86, -64.5) * mm});
            skLineSegment(sketch, "E74.58.0", {"start": v(111.8, -59.62) * mm, "end": v(110.85, -60.1) * mm});
            skLineSegment(sketch, "E74.58.1", {"start": v(111.8, -59.62) * mm, "end": v(112.67, -59.18) * mm});
            skLineSegment(sketch, "E74.58.2", {"start": v(112.94, -61.13) * mm, "end": v(113.6, -60.4) * mm});
            skLineSegment(sketch, "E74.58.3", {"start": v(112.94, -61.13) * mm, "end": v(112.21, -61.9) * mm});
            skLineSegment(sketch, "E74.59.0", {"start": v(109.7, -57.24) * mm, "end": v(108.8, -57.8) * mm});
            skLineSegment(sketch, "E74.59.1", {"start": v(109.7, -57.24) * mm, "end": v(110.53, -56.71) * mm});
            skLineSegment(sketch, "E74.59.2", {"start": v(110.98, -58.63) * mm, "end": v(111.57, -57.86) * mm});
            skLineSegment(sketch, "E74.59.3", {"start": v(110.98, -58.63) * mm, "end": v(110.33, -59.47) * mm});
            skLineSegment(sketch, "E74.60.0", {"start": v(107.4, -55.06) * mm, "end": v(106.56, -55.7) * mm});
            skLineSegment(sketch, "E74.60.1", {"start": v(107.4, -55.06) * mm, "end": v(108.18, -54.46) * mm});
            skLineSegment(sketch, "E74.60.2", {"start": v(108.8, -56.33) * mm, "end": v(109.32, -55.5) * mm});
            skLineSegment(sketch, "E74.60.3", {"start": v(108.8, -56.33) * mm, "end": v(108.23, -57.22) * mm});
            skLineSegment(sketch, "E74.61.0", {"start": v(104.9, -53.1) * mm, "end": v(104.13, -53.82) * mm});
            skLineSegment(sketch, "E74.61.1", {"start": v(104.9, -53.1) * mm, "end": v(105.62, -52.43) * mm});
            skLineSegment(sketch, "E74.61.2", {"start": v(106.41, -54.23) * mm, "end": v(106.86, -53.36) * mm});
            skLineSegment(sketch, "E74.61.3", {"start": v(106.41, -54.23) * mm, "end": v(105.93, -55.18) * mm});
            skLineSegment(sketch, "E74.62.0", {"start": v(102.24, -51.38) * mm, "end": v(101.54, -52.17) * mm});
            skLineSegment(sketch, "E74.62.1", {"start": v(102.24, -51.38) * mm, "end": v(102.9, -50.65) * mm});
            skLineSegment(sketch, "E74.62.2", {"start": v(103.85, -52.37) * mm, "end": v(104.2, -51.46) * mm});
            skLineSegment(sketch, "E74.62.3", {"start": v(103.85, -52.37) * mm, "end": v(103.45, -53.36) * mm});
            skLineSegment(sketch, "E74.63.0", {"start": v(99.43, -49.91) * mm, "end": v(98.8, -50.77) * mm});
            skLineSegment(sketch, "E74.63.1", {"start": v(99.43, -49.91) * mm, "end": v(100.01, -49.12) * mm});
            skLineSegment(sketch, "E74.63.2", {"start": v(101.12, -50.75) * mm, "end": v(101.4, -49.81) * mm});
            skLineSegment(sketch, "E74.63.3", {"start": v(101.12, -50.75) * mm, "end": v(100.82, -51.77) * mm});
            skLineSegment(sketch, "E74.64.0", {"start": v(96.5, -48.7) * mm, "end": v(95.94, -49.62) * mm});
            skLineSegment(sketch, "E74.64.1", {"start": v(96.5, -48.7) * mm, "end": v(97, -47.87) * mm});
            skLineSegment(sketch, "E74.64.2", {"start": v(98.25, -49.4) * mm, "end": v(98.44, -48.43) * mm});
            skLineSegment(sketch, "E74.64.3", {"start": v(98.25, -49.4) * mm, "end": v(98.05, -50.43) * mm});
            skLineSegment(sketch, "E74.65.0", {"start": v(93.46, -47.78) * mm, "end": v(93, -48.74) * mm});
            skLineSegment(sketch, "E74.65.1", {"start": v(93.46, -47.78) * mm, "end": v(93.89, -46.9) * mm});
            skLineSegment(sketch, "E74.65.2", {"start": v(95.27, -48.3) * mm, "end": v(95.37, -47.33) * mm});
            skLineSegment(sketch, "E74.65.3", {"start": v(95.27, -48.3) * mm, "end": v(95.17, -49.36) * mm});
            skLineSegment(sketch, "E74.66.0", {"start": v(90.35, -47.14) * mm, "end": v(89.98, -48.14) * mm});
            skLineSegment(sketch, "E74.66.1", {"start": v(90.35, -47.14) * mm, "end": v(90.7, -46.23) * mm});
            skLineSegment(sketch, "E74.66.2", {"start": v(92.2, -47.5) * mm, "end": v(92.22, -46.51) * mm});
            skLineSegment(sketch, "E74.66.3", {"start": v(92.2, -47.5) * mm, "end": v(92.2, -48.55) * mm});
            skLineSegment(sketch, "E74.67.0", {"start": v(87.2, -46.8) * mm, "end": v(86.92, -47.82) * mm});
            skLineSegment(sketch, "E74.67.1", {"start": v(87.2, -46.8) * mm, "end": v(87.46, -45.85) * mm});
            skLineSegment(sketch, "E74.67.2", {"start": v(89.08, -46.97) * mm, "end": v(89, -46) * mm});
            skLineSegment(sketch, "E74.67.3", {"start": v(89.08, -46.97) * mm, "end": v(89.17, -48.02) * mm});
            skArc(sketch, "E75", {"start": v(84.2, -45.77) * mm, "mid": v(84.97, -45.76) * mm, "end": v(85.75, -45.77) * mm});
            skArc(sketch, "E76", {"start": v(86.1, -47.78) * mm, "mid": v(86.51, -47.8) * mm, "end": v(86.92, -47.82) * mm});
            skArc(sketch, "E77.1.0", {"start": v(80.95, -46) * mm, "mid": v(81.72, -45.91) * mm, "end": v(82.49, -45.85) * mm});
            skArc(sketch, "E77.1.1", {"start": v(83.02, -47.82) * mm, "mid": v(83.44, -47.8) * mm, "end": v(83.85, -47.78) * mm});
            skArc(sketch, "E77.2.0", {"start": v(77.73, -46.51) * mm, "mid": v(78.49, -46.36) * mm, "end": v(79.25, -46.23) * mm});
            skArc(sketch, "E77.2.1", {"start": v(79.97, -48.14) * mm, "mid": v(80.37, -48.08) * mm, "end": v(80.78, -48.02) * mm});
            skArc(sketch, "E77.3.0", {"start": v(74.57, -47.33) * mm, "mid": v(75.31, -47.1) * mm, "end": v(76.06, -46.9) * mm});
            skArc(sketch, "E77.3.1", {"start": v(76.95, -48.74) * mm, "mid": v(77.35, -48.64) * mm, "end": v(77.75, -48.55) * mm});
            skArc(sketch, "E77.4.0", {"start": v(71.5, -48.43) * mm, "mid": v(72.22, -48.14) * mm, "end": v(72.94, -47.87) * mm});
            skArc(sketch, "E77.4.1", {"start": v(74, -49.62) * mm, "mid": v(74.4, -49.49) * mm, "end": v(74.78, -49.36) * mm});
            skArc(sketch, "E77.5.0", {"start": v(68.55, -49.81) * mm, "mid": v(69.24, -49.46) * mm, "end": v(69.93, -49.12) * mm});
            skArc(sketch, "E77.5.1", {"start": v(71.15, -50.77) * mm, "mid": v(71.52, -50.6) * mm, "end": v(71.9, -50.43) * mm});
            skArc(sketch, "E77.6.0", {"start": v(65.74, -51.46) * mm, "mid": v(66.4, -51.05) * mm, "end": v(67.05, -50.65) * mm});
            skArc(sketch, "E77.6.1", {"start": v(68.41, -52.17) * mm, "mid": v(68.77, -51.97) * mm, "end": v(69.13, -51.77) * mm});
            skArc(sketch, "E77.7.0", {"start": v(63.09, -53.36) * mm, "mid": v(63.7, -52.89) * mm, "end": v(64.32, -52.43) * mm});
            skArc(sketch, "E77.7.1", {"start": v(65.82, -53.82) * mm, "mid": v(66.15, -53.59) * mm, "end": v(66.5, -53.36) * mm});
            skArc(sketch, "E77.8.0", {"start": v(60.63, -55.5) * mm, "mid": v(61.2, -54.97) * mm, "end": v(61.77, -54.46) * mm});
            skArc(sketch, "E77.8.1", {"start": v(63.38, -55.7) * mm, "mid": v(63.7, -55.44) * mm, "end": v(64.02, -55.18) * mm});
            skArc(sketch, "E77.9.0", {"start": v(58.37, -57.86) * mm, "mid": v(58.89, -57.28) * mm, "end": v(59.41, -56.71) * mm});
            skArc(sketch, "E77.9.1", {"start": v(61.14, -57.8) * mm, "mid": v(61.43, -57.51) * mm, "end": v(61.72, -57.22) * mm});
            skArc(sketch, "E77.10.0", {"start": v(56.34, -60.4) * mm, "mid": v(56.8, -59.79) * mm, "end": v(57.28, -59.18) * mm});
            skArc(sketch, "E77.10.1", {"start": v(59.1, -60.1) * mm, "mid": v(59.35, -59.79) * mm, "end": v(59.62, -59.47) * mm});
            skArc(sketch, "E77.11.0", {"start": v(54.56, -63.14) * mm, "mid": v(54.96, -62.48) * mm, "end": v(55.37, -61.82) * mm});
            skArc(sketch, "E77.11.1", {"start": v(57.27, -62.58) * mm, "mid": v(57.5, -62.24) * mm, "end": v(57.74, -61.9) * mm});
            skArc(sketch, "E77.12.0", {"start": v(53.04, -66.02) * mm, "mid": v(53.37, -65.33) * mm, "end": v(53.73, -64.64) * mm});
            skArc(sketch, "E77.12.1", {"start": v(55.68, -65.22) * mm, "mid": v(55.88, -64.86) * mm, "end": v(56.08, -64.5) * mm});
            skArc(sketch, "E77.13.0", {"start": v(51.79, -69.03) * mm, "mid": v(52.06, -68.3) * mm, "end": v(52.34, -67.6) * mm});
            skArc(sketch, "E77.13.1", {"start": v(54.35, -67.99) * mm, "mid": v(54.51, -67.6) * mm, "end": v(54.68, -67.23) * mm});
            skArc(sketch, "E77.14.0", {"start": v(50.82, -72.14) * mm, "mid": v(51.02, -71.4) * mm, "end": v(51.24, -70.66) * mm});
            skArc(sketch, "E77.14.1", {"start": v(53.27, -70.87) * mm, "mid": v(53.4, -70.48) * mm, "end": v(53.53, -70.09) * mm});
            skArc(sketch, "E77.15.0", {"start": v(50.14, -75.33) * mm, "mid": v(50.27, -74.57) * mm, "end": v(50.42, -73.82) * mm});
            skArc(sketch, "E77.15.1", {"start": v(52.47, -73.84) * mm, "mid": v(52.56, -73.44) * mm, "end": v(52.65, -73.04) * mm});
            skArc(sketch, "E77.16.0", {"start": v(49.76, -78.57) * mm, "mid": v(49.82, -77.8) * mm, "end": v(49.9, -77.03) * mm});
            skArc(sketch, "E77.16.1", {"start": v(51.94, -76.87) * mm, "mid": v(52, -76.46) * mm, "end": v(52.05, -76.05) * mm});
            skArc(sketch, "E77.17.0", {"start": v(49.68, -81.83) * mm, "mid": v(49.67, -81.06) * mm, "end": v(49.68, -80.29) * mm});
            skArc(sketch, "E77.17.1", {"start": v(51.7, -79.93) * mm, "mid": v(51.7, -79.52) * mm, "end": v(51.73, -79.11) * mm});
            skArc(sketch, "E77.18.0", {"start": v(49.9, -85.09) * mm, "mid": v(49.82, -84.32) * mm, "end": v(49.76, -83.55) * mm});
            skArc(sketch, "E77.18.1", {"start": v(51.73, -83) * mm, "mid": v(51.7, -82.6) * mm, "end": v(51.7, -82.19) * mm});
            skArc(sketch, "E77.19.0", {"start": v(50.42, -88.3) * mm, "mid": v(50.27, -87.55) * mm, "end": v(50.14, -86.79) * mm});
            skArc(sketch, "E77.19.1", {"start": v(52.05, -86.07) * mm, "mid": v(52, -85.66) * mm, "end": v(51.94, -85.25) * mm});
            skArc(sketch, "E77.20.0", {"start": v(51.24, -91.46) * mm, "mid": v(51.02, -90.72) * mm, "end": v(50.82, -89.97) * mm});
            skArc(sketch, "E77.20.1", {"start": v(52.65, -89.08) * mm, "mid": v(52.56, -88.68) * mm, "end": v(52.47, -88.28) * mm});
            skArc(sketch, "E77.21.0", {"start": v(52.34, -94.53) * mm, "mid": v(52.06, -93.81) * mm, "end": v(51.79, -93.09) * mm});
            skArc(sketch, "E77.21.1", {"start": v(53.53, -92.03) * mm, "mid": v(53.4, -91.64) * mm, "end": v(53.27, -91.25) * mm});
            skArc(sketch, "E77.22.0", {"start": v(53.73, -97.48) * mm, "mid": v(53.37, -96.8) * mm, "end": v(53.04, -96.1) * mm});
            skArc(sketch, "E77.22.1", {"start": v(54.68, -94.89) * mm, "mid": v(54.51, -94.51) * mm, "end": v(54.35, -94.13) * mm});
            skArc(sketch, "E77.23.0", {"start": v(55.37, -100.3) * mm, "mid": v(54.96, -99.64) * mm, "end": v(54.56, -98.98) * mm});
            skArc(sketch, "E77.23.1", {"start": v(56.08, -97.62) * mm, "mid": v(55.88, -97.26) * mm, "end": v(55.68, -96.9) * mm});
            skArc(sketch, "E77.24.0", {"start": v(57.28, -102.94) * mm, "mid": v(56.8, -102.33) * mm, "end": v(56.34, -101.71) * mm});
            skArc(sketch, "E77.24.1", {"start": v(57.74, -100.22) * mm, "mid": v(57.5, -99.88) * mm, "end": v(57.27, -99.54) * mm});
            skArc(sketch, "E77.25.0", {"start": v(59.41, -105.4) * mm, "mid": v(58.89, -104.84) * mm, "end": v(58.37, -104.26) * mm});
            skArc(sketch, "E77.25.1", {"start": v(59.62, -102.65) * mm, "mid": v(59.35, -102.33) * mm, "end": v(59.1, -102.02) * mm});
            skArc(sketch, "E77.26.0", {"start": v(61.77, -107.66) * mm, "mid": v(61.2, -107.15) * mm, "end": v(60.63, -106.62) * mm});
            skArc(sketch, "E77.26.1", {"start": v(61.72, -104.9) * mm, "mid": v(61.43, -104.6) * mm, "end": v(61.14, -104.31) * mm});
            skArc(sketch, "E77.27.0", {"start": v(64.32, -109.69) * mm, "mid": v(63.7, -109.23) * mm, "end": v(63.09, -108.76) * mm});
            skArc(sketch, "E77.27.1", {"start": v(64.02, -106.94) * mm, "mid": v(63.7, -106.68) * mm, "end": v(63.38, -106.41) * mm});
            skArc(sketch, "E77.28.0", {"start": v(67.05, -111.47) * mm, "mid": v(66.4, -111.07) * mm, "end": v(65.74, -110.66) * mm});
            skArc(sketch, "E77.28.1", {"start": v(66.5, -108.76) * mm, "mid": v(66.15, -108.53) * mm, "end": v(65.82, -108.3) * mm});
            skArc(sketch, "E77.29.0", {"start": v(69.93, -113) * mm, "mid": v(69.24, -112.66) * mm, "end": v(68.55, -112.3) * mm});
            skArc(sketch, "E77.29.1", {"start": v(69.13, -110.35) * mm, "mid": v(68.77, -110.15) * mm, "end": v(68.41, -109.95) * mm});
            skArc(sketch, "E77.30.0", {"start": v(72.94, -114.25) * mm, "mid": v(72.22, -113.98) * mm, "end": v(71.5, -113.69) * mm});
            skArc(sketch, "E77.30.1", {"start": v(71.9, -111.69) * mm, "mid": v(71.52, -111.52) * mm, "end": v(71.15, -111.35) * mm});
            skArc(sketch, "E77.31.0", {"start": v(76.06, -115.22) * mm, "mid": v(75.31, -115.01) * mm, "end": v(74.57, -114.8) * mm});
            skArc(sketch, "E77.31.1", {"start": v(74.78, -112.76) * mm, "mid": v(74.4, -112.63) * mm, "end": v(74, -112.5) * mm});
            skArc(sketch, "E77.32.0", {"start": v(79.25, -115.9) * mm, "mid": v(78.49, -115.76) * mm, "end": v(77.73, -115.6) * mm});
            skArc(sketch, "E77.32.1", {"start": v(77.75, -113.57) * mm, "mid": v(77.35, -113.48) * mm, "end": v(76.95, -113.38) * mm});
            skArc(sketch, "E77.33.0", {"start": v(82.49, -116.27) * mm, "mid": v(81.72, -116.2) * mm, "end": v(80.95, -116.13) * mm});
            skArc(sketch, "E77.33.1", {"start": v(80.78, -114.1) * mm, "mid": v(80.37, -114.04) * mm, "end": v(79.97, -113.98) * mm});
            skArc(sketch, "E77.34.0", {"start": v(85.75, -116.35) * mm, "mid": v(84.97, -116.36) * mm, "end": v(84.2, -116.35) * mm});
            skArc(sketch, "E77.34.1", {"start": v(83.85, -114.34) * mm, "mid": v(83.44, -114.32) * mm, "end": v(83.02, -114.3) * mm});
            skArc(sketch, "E77.35.0", {"start": v(89, -116.13) * mm, "mid": v(88.23, -116.2) * mm, "end": v(87.46, -116.27) * mm});
            skArc(sketch, "E77.35.1", {"start": v(86.92, -114.3) * mm, "mid": v(86.51, -114.32) * mm, "end": v(86.1, -114.34) * mm});
            skArc(sketch, "E77.36.0", {"start": v(92.22, -115.6) * mm, "mid": v(91.46, -115.76) * mm, "end": v(90.7, -115.9) * mm});
            skArc(sketch, "E77.36.1", {"start": v(89.98, -113.98) * mm, "mid": v(89.57, -114.04) * mm, "end": v(89.17, -114.1) * mm});
            skArc(sketch, "E77.37.0", {"start": v(95.37, -114.8) * mm, "mid": v(94.63, -115.01) * mm, "end": v(93.89, -115.22) * mm});
            skArc(sketch, "E77.37.1", {"start": v(93, -113.38) * mm, "mid": v(92.6, -113.48) * mm, "end": v(92.2, -113.57) * mm});
            skArc(sketch, "E77.38.0", {"start": v(98.44, -113.69) * mm, "mid": v(97.73, -113.98) * mm, "end": v(97, -114.25) * mm});
            skArc(sketch, "E77.38.1", {"start": v(95.94, -112.5) * mm, "mid": v(95.56, -112.63) * mm, "end": v(95.17, -112.76) * mm});
            skArc(sketch, "E77.39.0", {"start": v(101.4, -112.3) * mm, "mid": v(100.7, -112.66) * mm, "end": v(100.01, -113) * mm});
            skArc(sketch, "E77.39.1", {"start": v(98.8, -111.35) * mm, "mid": v(98.42, -111.52) * mm, "end": v(98.05, -111.69) * mm});
            skArc(sketch, "E77.40.0", {"start": v(104.2, -110.66) * mm, "mid": v(103.56, -111.07) * mm, "end": v(102.9, -111.47) * mm});
            skArc(sketch, "E77.40.1", {"start": v(101.54, -109.95) * mm, "mid": v(101.18, -110.15) * mm, "end": v(100.82, -110.35) * mm});
            skArc(sketch, "E77.41.0", {"start": v(106.86, -108.76) * mm, "mid": v(106.25, -109.23) * mm, "end": v(105.62, -109.69) * mm});
            skArc(sketch, "E77.41.1", {"start": v(104.13, -108.3) * mm, "mid": v(103.8, -108.53) * mm, "end": v(103.45, -108.76) * mm});
            skArc(sketch, "E77.42.0", {"start": v(109.32, -106.62) * mm, "mid": v(108.75, -107.15) * mm, "end": v(108.18, -107.66) * mm});
            skArc(sketch, "E77.42.1", {"start": v(106.56, -106.41) * mm, "mid": v(106.25, -106.68) * mm, "end": v(105.93, -106.94) * mm});
            skArc(sketch, "E77.43.0", {"start": v(111.57, -104.26) * mm, "mid": v(111.06, -104.84) * mm, "end": v(110.53, -105.4) * mm});
            skArc(sketch, "E77.43.1", {"start": v(108.8, -104.31) * mm, "mid": v(108.52, -104.6) * mm, "end": v(108.23, -104.9) * mm});
            skArc(sketch, "E77.44.0", {"start": v(113.6, -101.71) * mm, "mid": v(113.14, -102.33) * mm, "end": v(112.67, -102.94) * mm});
            skArc(sketch, "E77.44.1", {"start": v(110.85, -102.02) * mm, "mid": v(110.6, -102.33) * mm, "end": v(110.33, -102.65) * mm});
            skArc(sketch, "E77.45.0", {"start": v(115.39, -98.98) * mm, "mid": v(114.99, -99.64) * mm, "end": v(114.57, -100.3) * mm});
            skArc(sketch, "E77.45.1", {"start": v(112.68, -99.54) * mm, "mid": v(112.45, -99.88) * mm, "end": v(112.21, -100.22) * mm});
            skArc(sketch, "E77.46.0", {"start": v(116.9, -96.1) * mm, "mid": v(116.57, -96.8) * mm, "end": v(116.22, -97.48) * mm});
            skArc(sketch, "E77.46.1", {"start": v(114.26, -96.9) * mm, "mid": v(114.06, -97.26) * mm, "end": v(113.86, -97.62) * mm});
            skArc(sketch, "E77.47.0", {"start": v(118.16, -93.09) * mm, "mid": v(117.89, -93.81) * mm, "end": v(117.6, -94.53) * mm});
            skArc(sketch, "E77.47.1", {"start": v(115.6, -94.13) * mm, "mid": v(115.44, -94.51) * mm, "end": v(115.27, -94.89) * mm});
            skArc(sketch, "E77.48.0", {"start": v(119.13, -89.97) * mm, "mid": v(118.93, -90.72) * mm, "end": v(118.7, -91.46) * mm});
            skArc(sketch, "E77.48.1", {"start": v(116.68, -91.25) * mm, "mid": v(116.55, -91.64) * mm, "end": v(116.41, -92.03) * mm});
            skArc(sketch, "E77.49.0", {"start": v(119.8, -86.79) * mm, "mid": v(119.67, -87.55) * mm, "end": v(119.52, -88.3) * mm});
            skArc(sketch, "E77.49.1", {"start": v(117.48, -88.28) * mm, "mid": v(117.39, -88.68) * mm, "end": v(117.3, -89.08) * mm});
            skArc(sketch, "E77.50.0", {"start": v(120.19, -83.55) * mm, "mid": v(120.12, -84.32) * mm, "end": v(120.04, -85.09) * mm});
            skArc(sketch, "E77.50.1", {"start": v(118, -85.25) * mm, "mid": v(117.95, -85.66) * mm, "end": v(117.9, -86.07) * mm});
            skArc(sketch, "E77.51.0", {"start": v(120.26, -80.29) * mm, "mid": v(120.27, -81.06) * mm, "end": v(120.26, -81.83) * mm});
            skArc(sketch, "E77.51.1", {"start": v(118.25, -82.19) * mm, "mid": v(118.24, -82.6) * mm, "end": v(118.22, -83) * mm});
            skArc(sketch, "E77.52.0", {"start": v(120.04, -77.03) * mm, "mid": v(120.12, -77.8) * mm, "end": v(120.19, -78.57) * mm});
            skArc(sketch, "E77.52.1", {"start": v(118.22, -79.11) * mm, "mid": v(118.24, -79.52) * mm, "end": v(118.25, -79.93) * mm});
            skArc(sketch, "E77.53.0", {"start": v(119.52, -73.82) * mm, "mid": v(119.67, -74.57) * mm, "end": v(119.8, -75.33) * mm});
            skArc(sketch, "E77.53.1", {"start": v(117.9, -76.05) * mm, "mid": v(117.95, -76.46) * mm, "end": v(118, -76.87) * mm});
            skArc(sketch, "E77.54.0", {"start": v(118.7, -70.66) * mm, "mid": v(118.93, -71.4) * mm, "end": v(119.13, -72.14) * mm});
            skArc(sketch, "E77.54.1", {"start": v(117.3, -73.04) * mm, "mid": v(117.39, -73.44) * mm, "end": v(117.48, -73.84) * mm});
            skArc(sketch, "E77.55.0", {"start": v(117.6, -67.6) * mm, "mid": v(117.89, -68.3) * mm, "end": v(118.16, -69.03) * mm});
            skArc(sketch, "E77.55.1", {"start": v(116.41, -70.09) * mm, "mid": v(116.55, -70.48) * mm, "end": v(116.68, -70.87) * mm});
            skArc(sketch, "E77.56.0", {"start": v(116.22, -64.64) * mm, "mid": v(116.57, -65.33) * mm, "end": v(116.9, -66.02) * mm});
            skArc(sketch, "E77.56.1", {"start": v(115.27, -67.23) * mm, "mid": v(115.44, -67.6) * mm, "end": v(115.6, -67.99) * mm});
            skArc(sketch, "E77.57.0", {"start": v(114.57, -61.82) * mm, "mid": v(114.99, -62.48) * mm, "end": v(115.39, -63.14) * mm});
            skArc(sketch, "E77.57.1", {"start": v(113.86, -64.5) * mm, "mid": v(114.06, -64.86) * mm, "end": v(114.26, -65.22) * mm});
            skArc(sketch, "E77.58.0", {"start": v(112.67, -59.18) * mm, "mid": v(113.14, -59.79) * mm, "end": v(113.6, -60.4) * mm});
            skArc(sketch, "E77.58.1", {"start": v(112.21, -61.9) * mm, "mid": v(112.45, -62.24) * mm, "end": v(112.68, -62.58) * mm});
            skArc(sketch, "E77.59.0", {"start": v(110.53, -56.71) * mm, "mid": v(111.06, -57.28) * mm, "end": v(111.57, -57.86) * mm});
            skArc(sketch, "E77.59.1", {"start": v(110.33, -59.47) * mm, "mid": v(110.6, -59.79) * mm, "end": v(110.85, -60.1) * mm});
            skArc(sketch, "E77.60.0", {"start": v(108.18, -54.46) * mm, "mid": v(108.75, -54.97) * mm, "end": v(109.32, -55.5) * mm});
            skArc(sketch, "E77.60.1", {"start": v(108.23, -57.22) * mm, "mid": v(108.52, -57.51) * mm, "end": v(108.8, -57.8) * mm});
            skArc(sketch, "E77.61.0", {"start": v(105.62, -52.43) * mm, "mid": v(106.25, -52.89) * mm, "end": v(106.86, -53.36) * mm});
            skArc(sketch, "E77.61.1", {"start": v(105.93, -55.18) * mm, "mid": v(106.25, -55.44) * mm, "end": v(106.56, -55.7) * mm});
            skArc(sketch, "E77.62.0", {"start": v(102.9, -50.65) * mm, "mid": v(103.56, -51.05) * mm, "end": v(104.2, -51.46) * mm});
            skArc(sketch, "E77.62.1", {"start": v(103.45, -53.36) * mm, "mid": v(103.8, -53.59) * mm, "end": v(104.13, -53.82) * mm});
            skArc(sketch, "E77.63.0", {"start": v(100.01, -49.12) * mm, "mid": v(100.7, -49.46) * mm, "end": v(101.4, -49.81) * mm});
            skArc(sketch, "E77.63.1", {"start": v(100.82, -51.77) * mm, "mid": v(101.18, -51.97) * mm, "end": v(101.54, -52.17) * mm});
            skArc(sketch, "E77.64.0", {"start": v(97, -47.87) * mm, "mid": v(97.73, -48.14) * mm, "end": v(98.44, -48.43) * mm});
            skArc(sketch, "E77.64.1", {"start": v(98.05, -50.43) * mm, "mid": v(98.42, -50.6) * mm, "end": v(98.8, -50.77) * mm});
            skArc(sketch, "E77.65.0", {"start": v(93.89, -46.9) * mm, "mid": v(94.63, -47.1) * mm, "end": v(95.37, -47.33) * mm});
            skArc(sketch, "E77.65.1", {"start": v(95.17, -49.36) * mm, "mid": v(95.56, -49.49) * mm, "end": v(95.94, -49.62) * mm});
            skArc(sketch, "E77.66.0", {"start": v(90.7, -46.23) * mm, "mid": v(91.46, -46.36) * mm, "end": v(92.22, -46.51) * mm});
            skArc(sketch, "E77.66.1", {"start": v(92.2, -48.55) * mm, "mid": v(92.6, -48.64) * mm, "end": v(93, -48.74) * mm});
            skArc(sketch, "E77.67.0", {"start": v(87.46, -45.85) * mm, "mid": v(88.23, -45.91) * mm, "end": v(89, -46) * mm});
            skArc(sketch, "E77.67.1", {"start": v(89.17, -48.02) * mm, "mid": v(89.57, -48.08) * mm, "end": v(89.98, -48.14) * mm});
            skSolve(sketch);
        }
        {
            var Q0;
            {var subQ0=sQuery(id+"F0.wireOp",EDGE,"E32");Q0=makeQuery(id+"F0.imprint","IMPRINT",FACE,{"disambiguationData":[TD([[makeQuery(id+"F0.imprint","IMPRINT",EDGE,{"derivedFrom":subQ0}),1.0]])]});}
            var Q1;
            Q1=makeQuery(id+"F0.imprint","IMPRINT",FACE,{"disambiguationData":[TD([[makeQuery(id+"F0.imprint","IMPRINT",EDGE,{"derivedFrom":sQuery(id+"F0.wireOp",EDGE,"E48")}),1.0]])]});
            var Q2;
            Q2=makeQuery(id+"F0.imprint","IMPRINT",FACE,{"disambiguationData":[TD([[makeQuery(id+"F0.imprint","IMPRINT",EDGE,{"derivedFrom":sQuery(id+"F0.wireOp",EDGE,"E64")}),1.0]])]});
            extrude(context, id + "F1", {"entities" : qUnion([Q0, Q1, Q2]), "depth" : 5 * mm});
        }
    });
